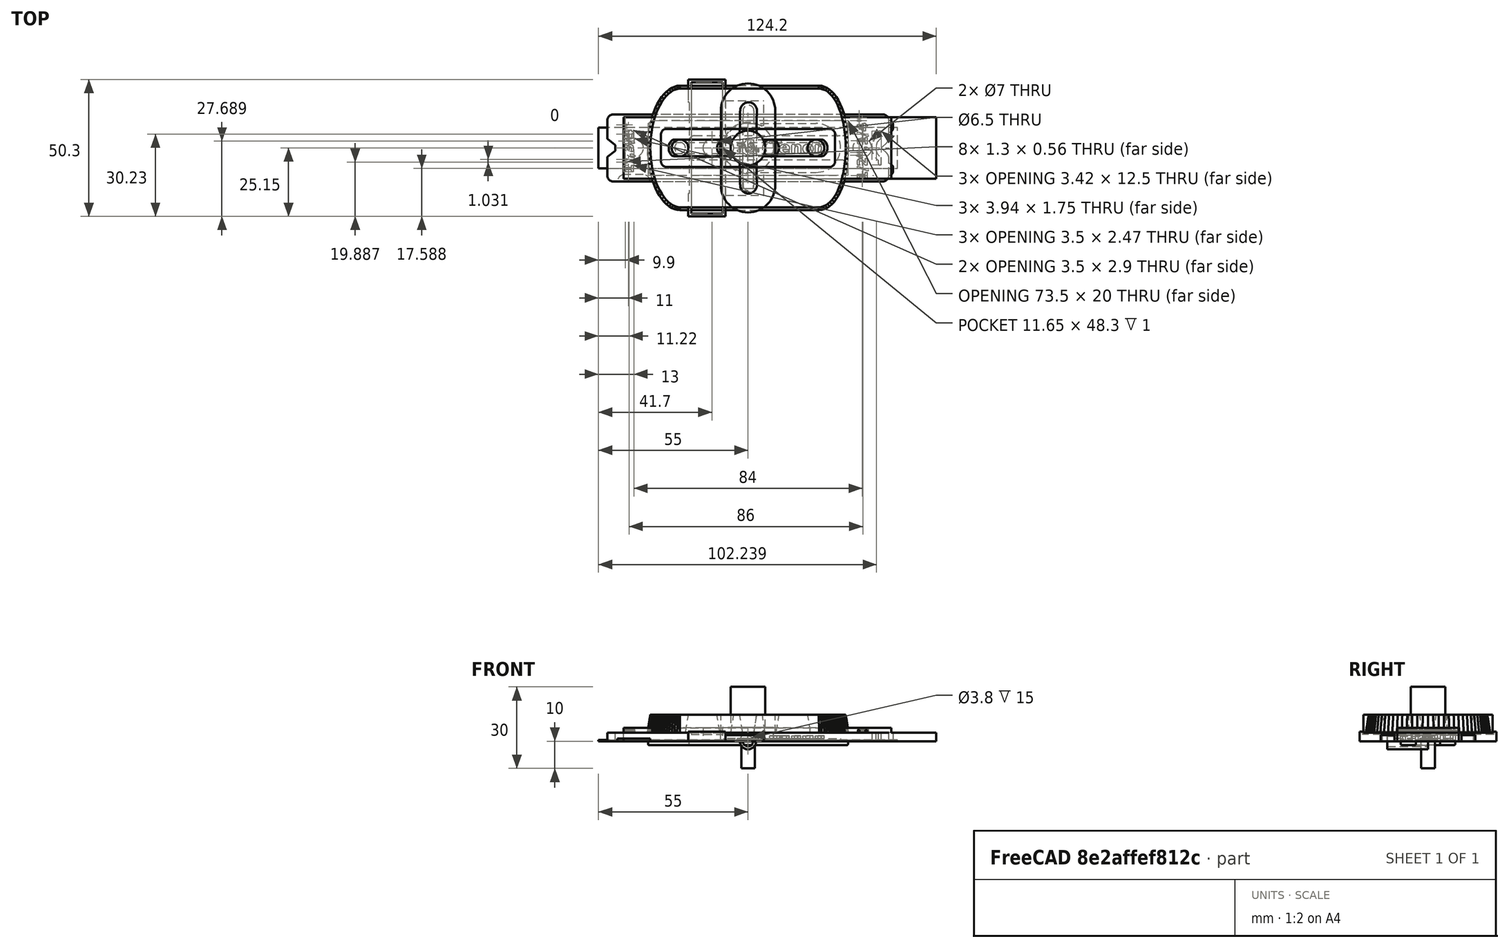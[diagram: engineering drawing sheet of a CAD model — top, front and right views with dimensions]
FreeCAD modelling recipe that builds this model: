
FCSTD DOCUMENT  (FreeCAD 1.1R20260325 (Git shallow))
Label: FMT Guide
License: All rights reserved
LicenseURL: http://en.wikipedia.org/wiki/All_rights_reserved
objects: Sketcher::SketchObject×25, PartDesign::Pad×16, App::Point×10, PartDesign::Body×10, PartDesign::Pocket×5, Part::Part2DObjectPython×4, Part::Extrusion×4, Part::Fuse×3, Part::MultiFuse×3, PartDesign::Plane×2, Part::Cut×2, Mesh::Feature×2, Spreadsheet::Sheet×1, Part::DatumPlane×1, PartDesign::Fillet×1, Part::Scale×1, Part::Loft×1, PartDesign::LinearPattern×1
note: 148 computed .brp shape members not serialized (recipe doc carries the construction recipe); baked Part::Feature solids carry a one-line shape summary decoded from their .brp

FEATURE [Sketcher::SketchObject] Sketch  label="Base Outline"
  ArcFitTolerance = 1e-06
  AttachmentSupport = -> [XY_Plane]
  ExternalTypes = [0]
  FullyConstrained = true
  MakeInternals = false
  MapMode = 5
  _ExternalGeoVersion = 0
  expr: Constraints[12] = Spreadsheet.Base_Corner_Radious
  expr: Constraints[18] = Spreadsheet.Base_Width
  expr: Constraints[19] = Spreadsheet.Base_Length
  sketch-geometry (32):
    g0: LineSegment StartX=-49.55 StartY=-12.32 StartZ=0 EndX=49.55 EndY=-12.32 EndZ=0
    g1: LineSegment [constr] StartX=51.75 StartY=-10.12 StartZ=0 EndX=51.75 EndY=10.12 EndZ=0
    g2: LineSegment StartX=49.55 StartY=12.32 StartZ=0 EndX=-49.55 EndY=12.32 EndZ=0
    g3: ArcOfCircle CenterX=-49.55 CenterY=10.12 CenterZ=0 NormalX=0 NormalY=0 NormalZ=1 AngleXU=0 Radius=2.2 StartAngle=1.5708 EndAngle=3.14159
    g4: ArcOfCircle CenterX=-49.55 CenterY=-10.12 CenterZ=0 NormalX=0 NormalY=0 NormalZ=1 AngleXU=0 Radius=2.2 StartAngle=3.14159 EndAngle=4.71239
    g5: ArcOfCircle CenterX=49.55 CenterY=-10.12 CenterZ=0 NormalX=0 NormalY=0 NormalZ=1 AngleXU=0 Radius=2.2 StartAngle=4.71239 EndAngle=6.28319
    g6: ArcOfCircle CenterX=49.55 CenterY=10.12 CenterZ=0 NormalX=0 NormalY=0 NormalZ=1 AngleXU=0 Radius=2.2 StartAngle=4e-16 EndAngle=1.5708
    g7: GeomPoint [constr] X=51.75 Y=-12.32 Z=0
    g8: LineSegment StartX=51.75 StartY=10.12 StartZ=0 EndX=51.75 EndY=3.625 EndZ=0
    g9: LineSegment StartX=51.75 StartY=-10.12 StartZ=0 EndX=51.75 EndY=-3.625 EndZ=0
    g10: ArcOfCircle CenterX=-49.55 CenterY=3.61127 CenterZ=0 NormalX=0 NormalY=0 NormalZ=1 AngleXU=0 Radius=2.2 StartAngle=3.14159 EndAngle=3.92699
    g11: ArcOfCircle CenterX=-49.55 CenterY=-3.61127 CenterZ=0 NormalX=0 NormalY=0 NormalZ=1 AngleXU=0 Radius=2.2 StartAngle=2.35619 EndAngle=3.14159
    g12: LineSegment StartX=51.5641 StartY=3.23597 StartZ=0 EndX=48.9359 EndY=1.11403 EndZ=0
    g13: LineSegment StartX=48.75 StartY=0.725 StartZ=0 EndX=48.75 EndY=-0.725 EndZ=0
    g14: LineSegment StartX=48.9359 StartY=-1.11403 StartZ=0 EndX=51.5641 EndY=-3.23597 EndZ=0
    g15: ArcOfCircle CenterX=51.25 CenterY=3.625 CenterZ=0 NormalX=0 NormalY=0 NormalZ=1 AngleXU=0 Radius=0.5 StartAngle=5.39161 EndAngle=6.28319
    g16: ArcOfCircle CenterX=51.25 CenterY=-3.625 CenterZ=0 NormalX=0 NormalY=0 NormalZ=1 AngleXU=0 Radius=0.5 StartAngle=6.28319 EndAngle=7.17476
    g17: ArcOfCircle CenterX=49.25 CenterY=-0.725 CenterZ=0 NormalX=0 NormalY=0 NormalZ=1 AngleXU=0 Radius=0.5 StartAngle=3.14159 EndAngle=4.03317
    g18: ArcOfCircle CenterX=49.25 CenterY=0.725 CenterZ=0 NormalX=0 NormalY=0 NormalZ=1 AngleXU=0 Radius=0.5 StartAngle=2.25002 EndAngle=3.14159
    g19: LineSegment StartX=-51.1056 StartY=2.05563 StartZ=0 EndX=-49.05 EndY=0 EndZ=0
    g20: LineSegment StartX=-49.05 StartY=0 StartZ=0 EndX=-51.1056 EndY=-2.05563 EndZ=0
    g21: LineSegment StartX=-48.95 StartY=5.75 StartZ=0 EndX=-48.95 EndY=3.5 EndZ=0
    g22: LineSegment StartX=-47.95 StartY=5.75 StartZ=0 EndX=-47.95 EndY=4.6 EndZ=0
    g23: ArcOfCircle CenterX=-48.45 CenterY=5.75 CenterZ=0 NormalX=0 NormalY=0 NormalZ=1 AngleXU=0 Radius=0.5 StartAngle=1e-16 EndAngle=3.14159
    g24: LineSegment StartX=-48.95 StartY=-3.5 StartZ=0 EndX=-48.95 EndY=-5.75 EndZ=0
    g25: LineSegment StartX=-47.95 StartY=-4.6 StartZ=0 EndX=-47.95 EndY=-5.75 EndZ=0
    g26: ArcOfCircle CenterX=-48.45 CenterY=-5.75 CenterZ=0 NormalX=0 NormalY=0 NormalZ=1 AngleXU=0 Radius=0.5 StartAngle=3.14159 EndAngle=6.28319
    g27: ArcOfCircle CenterX=-51.1056 CenterY=0 CenterZ=0 NormalX=0 NormalY=0 NormalZ=1 AngleXU=0 Radius=4.11057 StartAngle=5.26441 EndAngle=7.30196
    g28: ArcOfCircle CenterX=-51.1056 CenterY=0 CenterZ=0 NormalX=0 NormalY=0 NormalZ=1 AngleXU=0 Radius=5.57835 StartAngle=5.31366 EndAngle=7.25271
    g29: LineSegment StartX=-51.75 StartY=10.12 StartZ=0 EndX=-51.75 EndY=3.61127 EndZ=0
    g30: LineSegment StartX=-51.75 StartY=-3.61127 StartZ=0 EndX=-51.75 EndY=-10.12 EndZ=0
    g31: GeomPoint X=50.25 Y=2.175 Z=0
  constraints (79):
    c: Tangent(g0,g4) = -1.5708
    c: Tangent(g0,g5) = -1.5708
    c: Tangent(g1,g5) = -1.5708
    c: Tangent(g1,g6) = -1.5708
    c: Tangent(g2,g6) = -1.5708
    c: Tangent(g2,g3) = -1.5708
    c: Vertical(g1)
    c: Horizontal(g0)
    c: Horizontal(g2)
    c: Equal(g4,g5)
    c: PointOnObject(g7,g0)
    c: PointOnObject(g7,g1)
    c: Radius(g6) = 2.2
    c: Symmetric(g3,g6,g-2)
    c: Symmetric(g3,g4,g-1)
    c: Tangent(g6,g8)
    c: Coincident(g9,g1)
    c: Coincident(g8,g1)
    c: DistanceY(g0,g2) = 24.64
    c: DistanceX(g3,g1) = 103.5
    c: Equal(g3,g10)
    c: Tangent(g8,g15) = 1.5708
    c: Tangent(g12,g15) = 1.5708
    c: Tangent(g9,g16) = -1.5708
    c: Tangent(g14,g16) = 1.5708
    c: Tangent(g13,g17) = -1.5708
    c: Tangent(g14,g17) = -1.5708
    c: Tangent(g12,g18) = -1.5708
    c: Tangent(g13,g18) = -1.5708
    c: Equal(g15,g18)
    c: Equal(g18,g17)
    c: Equal(g17,g16)
    c: Radius(g15) = 0.5
    c: Symmetric(g18,g17,g-1)
    c: Symmetric(g15,g16,g-1)
    c: DistanceY(g16,g15) = 7.25
    c: DistanceY(g17,g18) = 1.45
    c: DistanceX(g18,g15) = 2
    c: Equal(g5,g6)
    c: PointOnObject(g19,g-1)
    c: Coincident(g20,g19)
    c: Angle(g19,g20) = 1.5708
    c: Tangent(g19,g10) = -1.5708
    c: Tangent(g20,g11) = -1.5708
    c: Symmetric(g10,g11,g-1)
    c: DistanceX(g10,g19) = 2.7
    c: Vertical(g21)
    c: Vertical(g22)
    c: Tangent(g23,g21) = -1.5708
    c: Tangent(g23,g22) = 1.5708
    c: Vertical(g22,g25)
    c: Vertical(g21,g24)
    c: Radius(g23) = 0.5
    c: Vertical(g24)
    c: Vertical(g25)
    c: Coincident(g26,g24)
    c: Coincident(g26,g25)
    c: Equal(g26,g23)
    c: Symmetric(g26,g23,g-1)
    c: Coincident(g27,g21)
    c: Coincident(g24,g27)
    c: PointOnObject(g27,g-1)
    c: Coincident(g28,g22)
    c: Coincident(g28,g25)
    c: Coincident(g27,g28)
    c: DistanceY(g26,g23) = 11.5
    c: DistanceX(g10,g23) = 3.3
    c: DistanceY(g21,g22) = 1.1
    c: DistanceY(g24,g21) = 7
    c: Vertical(g10,g27)
    c: Vertical(g30)
    c: Vertical(g29)
    c: Tangent(g10,g29) = -1.5708
    c: Tangent(g30,g11) = -1.5708
    c: Tangent(g3,g29) = -1.5708
    c: Tangent(g30,g4) = -1.5708
    c: DistanceY(g18,g15) = 2.9
    c: DistanceX(g19,g13) = 97.8
    c: Symmetric(g12,g12,g31)
FEATURE [Spreadsheet::Sheet] Spreadsheet
  cells = A1='Base; A2='Upper Title; B2(Upper_Title)='1",3/4"; A3='Lower Title; B3(Lower_Title)='1/2",1/4"; A4='Base Width; B4(Base_Width)=24.64; C4='Width of base of guide; A5='Base Length; B5(Base_Length)=103.5; C5='Length of base of guide; A6='Base Thickness; B6(Base_Thickness)=3.1; C6='Thickness of base of guide; A7='Base Corner Radious; B7(Base_Corner_Radious)=2.2; C7='Radii of base curves; A9='Lower Plane; B9(Lower_Plane)==Base_Thickness + 0.1; C9='Lower plane of guide portion; A10='Upper Plane; B10(Upper_Plane)==Lower_Plane + 6.5; C10='Upper plane of guide portion; A12='Pin Bottom Width; B12(Pin_Bottom_Width)=4; C12='Diameter of narrow point of Pin; A13='Pin Top Width; B13(Pin_Top_Width)=5; C13='Diameter of wide point of pin; A14='Pin Angle; B14(Pin_Angle)=9.22; A15='Calculated Pin Angle; B15==atan((Pin_Top_Width - Pin_Bottom_Width) / 3) / 2; A16='Bump Thickness; B16(Bump_Thickness)==Base_Thickness - 0.5; A17='Bump Width; B17(Bump_Width)=3.2; A18='Bump Spacing; B18(Bump_Spacing)=15.7; A19='Margin; B19(Margin)=1; A20='Pin Spacing; B20(Pin_Spacing)=250; A22='Mortise & Tenon; A23='Movement Ratio; B23(Movement_Ratio)=2; C23='Y-scale for guide; A24='Width; B24(Width)=12; C24='Width of tenon/mortise; A25='Length; B25(Length)=65; C25='Length of tenon/mortise; A26='Router Diameter; B26(Router_Diameter)==Width; C26='Always equals width of tenon; A27='Width Delta; B27(Width_Delta)=0; C27='Extra Tenon Width; A28='Length Delta; B28(Length_Delta)=0; C28='Extra Tenon Length; A29='Slot Delta; B29(Slot_Delta)=1.35; C29='Extra Mortise Length; A31='Dowel Centres; A32='Dowel Extent; B32(Dowel_Extent)=50; C32='Extent of Dowels; A33='Dowel Length; B33(Dowel_Length)==Dowel_Extent + 10; C33='Length of base (calculated); A34='Dowel Width; B34(Dowel_Width)=10; C34='Width of base; A35='Dowel Number; B35(Dowel_Number)=4; A37='Centering Disk; A38='Centering Title; B38(Centering_Title)='1/2"; A39='Centering Disk Diameter; B39(Centering_Disk_Diameter)=18.8; A40='Centering Disk Thickness; B40(Centering_Disk_Thickness)=5; A41='Centering Post Diameter; B41(Centering_Post_Diameter)=12.7; A42='Centering Post Length; B42(Centering_Post_Length)=10; A44='Y Tenon; A45='Tenon Base Width; B45(Tenon_Base_Width)=20; A46='Tenon Extra Length; B46(Tenon_Extra_Length)=20; A47='Y Tenon Length; B47(Y_Tenon_Length)=25.4; C47='Length of Y tenon; A48='Y Tenon Width; B48(Y_Tenon_Width)=12.7; C48='Width of tenon/Router Bit; A49='Y Slot Delta; B49(Y_Slot_Delta)=1; C49='Extra Mortise Length
FEATURE [PartDesign::Plane] DatumPlane  label="Upper Plane"
  AttachmentOffset = pos=(0,0,9.7) rot=(0,0,1;0rad)
  AttachmentSupport = -> [XY_Plane]
  Length = 60
  MapMode = 5
  Placement = pos=(0,0,9.7) rot=(0,0,1;0rad)
  ResizeMode = 0
  Width = 60
  expr: .AttachmentOffset.Base.z = Spreadsheet.Upper_Plane
FEATURE [PartDesign::Plane] DatumPlane001  label="Mid Plane"
  AttachmentOffset = pos=(0,0,3.2) rot=(0,0,1;0rad)
  AttachmentSupport = -> [XY_Plane]
  Length = 60
  MapMode = 5
  Placement = pos=(0,0,3.2) rot=(0,0,1;0rad)
  ResizeMode = 0
  Width = 60
  expr: .AttachmentOffset.Base.z = Spreadsheet.Lower_Plane
FEATURE [Part::DatumPlane] DatumPlane002  label="Base Surface Plane"
  AttachmentSupport = -> [Origin]
  Placement = pos=(0,0,3.1) rot=(0,0,1;0rad)
  expr: .Placement.Base.z = Spreadsheet.Base_Thickness
FEATURE [PartDesign::Pad] Pad  label="Base Base"
  Direction = (0,0,1)
  Length = 3.1
  Length2 = 10
  Profile = -> Sketch
  ReferenceAxis = -> Sketch [N_Axis]
  SideType = 0
  Suppressed = false
  Type = 0
  Type2 = 0
  expr: Length = Spreadsheet.Base_Thickness
FEATURE [Part::Part2DObjectPython] ShapeString001  label="Label"  # Draft 2D object (typed FeaturePython)
  FontFile = <path>
  Fuse = false
  Justification = 4
  JustificationReference = 0
  KeepLeftMargin = false
  MakeFace = true
  ObliqueAngle = 0
  Placement = pos=(44,0,3.1) rot=(0,0,1;4.71239rad)
  ScaleToSize = true
  Size = 3.5
  String = 1",3/4"
  Tracking = 0
  expr: .Placement.Base.z = Spreadsheet.Base_Thickness
  expr: String = Spreadsheet.Upper_Title
FEATURE [Part::Extrusion] Extrude  label="Extrude Upper"
  Base = -> ShapeString001
  Dir = (0,0,1)
  DirMode = 2
  FaceMakerClass = Part::FaceMakerBullseye
  FaceMakerMode = 3
  InnerWireTaper = 0
  LengthFwd = 1
  LengthRev = 0
  Solid = false
  Symmetric = false
FEATURE [App::Point] Origin007  label="Origin008"
  Role = Origin
FEATURE [Sketcher::SketchObject] Sketch008
  ArcFitTolerance = 1e-06
  AttachmentSupport = -> [Origin006]
  ExternalTypes = [0]
  FullyConstrained = true
  MakeInternals = false
  MapMode = 5
  _ExternalGeoVersion = 1
  expr: Constraints[1] = Spreadsheet.Centering_Disk_Diameter
  sketch-geometry (1):
    g0: Circle CenterX=0 CenterY=0 CenterZ=0 NormalX=0 NormalY=0 NormalZ=1 AngleXU=0 Radius=9.4
  constraints (2):
    c: Coincident(g0,g-1)
    c: Diameter(g0) = 18.8
FEATURE [PartDesign::Pad] Pad002  label="Base001"
  Direction = (0,0,1)
  Length = 5
  Length2 = 10
  Profile = -> Sketch008
  ReferenceAxis = -> Sketch008 [N_Axis]
  SideType = 0
  Suppressed = false
  Type = 0
  Type2 = 0
  expr: Length = Spreadsheet.Centering_Disk_Thickness
FEATURE [Sketcher::SketchObject] Sketch009
  ArcFitTolerance = 1e-06
  AttachmentSupport = -> [Pad002]
  ExternalTypes = [0]
  FullyConstrained = true
  MakeInternals = false
  MapMode = 5
  Placement = pos=(0,0,5) rot=(0,0,1;0rad)
  _ExternalGeoVersion = 1
  expr: Constraints[1] = Spreadsheet.Centering_Post_Diameter
  sketch-geometry (1):
    g0: Circle CenterX=0 CenterY=0 CenterZ=0 NormalX=0 NormalY=0 NormalZ=1 AngleXU=0 Radius=6.35
  constraints (2):
    c: Coincident(g0,g-1)
    c: Diameter(g0) = 12.7
FEATURE [PartDesign::Pad] Pad003  label="Arbor"
  BaseFeature = -> Pad002
  Direction = (0,0,1)
  Length = 15
  Length2 = 10
  Profile = -> Sketch009
  ReferenceAxis = -> Sketch009 [N_Axis]
  SideType = 0
  Suppressed = false
  Type = 0
  Type2 = 0
  expr: Length = Spreadsheet.Centering_Post_Length + Spreadsheet.Centering_Disk_Thickness
FEATURE [PartDesign::Body] Body003  label="Centering Bare"
  AllowCompound = false
  Group = -> [Sketch008,Pad002,Sketch009,Pad003]
  Origin = -> Origin006
  Tip = -> Pad003
FEATURE [Sketcher::SketchObject] Sketch013  label="Outline"
  ArcFitTolerance = 1e-06
  AttachmentSupport = -> [DatumPlane002]
  ExternalTypes = [0]
  FullyConstrained = true
  MakeInternals = false
  MapMode = 5
  Placement = pos=(0,0,3.1) rot=(0,0,1;0rad)
  _ExternalGeoVersion = 1
  expr: Constraints[18] = Spreadsheet.Dowel_Length
  expr: Constraints[19] = Spreadsheet.Dowel_Width
  sketch-geometry (10):
    g0: LineSegment StartX=-32 StartY=5 StartZ=0 EndX=-32 EndY=-5 EndZ=0
    g1: LineSegment StartX=-30 StartY=-7 StartZ=0 EndX=30 EndY=-7 EndZ=0
    g2: LineSegment StartX=32 StartY=-5 StartZ=0 EndX=32 EndY=5 EndZ=0
    g3: LineSegment StartX=30 StartY=7 StartZ=0 EndX=-30 EndY=7 EndZ=0
    g4: ArcOfCircle CenterX=-30 CenterY=5 CenterZ=0 NormalX=0 NormalY=0 NormalZ=1 AngleXU=0 Radius=2 StartAngle=1.5708 EndAngle=3.14159
    g5: ArcOfCircle CenterX=-30 CenterY=-5 CenterZ=0 NormalX=0 NormalY=0 NormalZ=1 AngleXU=0 Radius=2 StartAngle=3.14159 EndAngle=4.71239
    g6: ArcOfCircle CenterX=30 CenterY=-5 CenterZ=0 NormalX=0 NormalY=0 NormalZ=1 AngleXU=0 Radius=2 StartAngle=4.71239 EndAngle=6.28319
    g7: ArcOfCircle CenterX=30 CenterY=5 CenterZ=0 NormalX=0 NormalY=0 NormalZ=1 AngleXU=0 Radius=2 StartAngle=1e-16 EndAngle=1.5708
    g8: GeomPoint [constr] X=-32 Y=7 Z=0
    g9: GeomPoint [constr] X=32 Y=-7 Z=0
  constraints (22):
    c: Tangent(g0,g4) = -1.5708
    c: Tangent(g0,g5) = -1.5708
    c: Tangent(g1,g5) = -1.5708
    c: Tangent(g1,g6) = -1.5708
    c: Tangent(g2,g6) = -1.5708
    c: Tangent(g2,g7) = -1.5708
    c: Tangent(g3,g7) = -1.5708
    c: Tangent(g3,g4) = -1.5708
    c: Vertical(g0)
    c: Vertical(g2)
    c: Horizontal(g1)
    c: Horizontal(g3)
    c: Equal(g4,g5)
    c: PointOnObject(g8,g0)
    c: PointOnObject(g8,g3)
    c: PointOnObject(g9,g1)
    c: PointOnObject(g9,g2)
    c: Radius(g7) = 2
    c: DistanceX(g4,g7) = 60
    c: DistanceY(g6,g7) = 10
    c: Symmetric(g7,g6,g-1)
    c: Symmetric(g4,g7,g-2)
FEATURE [PartDesign::Pad] Pad004  label="Dowel Base"
  Direction = (0,0,1)
  Length = 6.6
  Length2 = 10
  Placement = pos=(0,0,3.1) rot=(0,0,1;0rad)
  Profile = -> Sketch013
  ReferenceAxis = -> Sketch013 [N_Axis]
  SideType = 0
  Suppressed = false
  Type = 0
  Type2 = 0
  expr: Length = Spreadsheet.Upper_Plane - Spreadsheet.Base_Thickness
FEATURE [App::Point] Origin009  label="Origin011"
  Role = Origin
FEATURE [App::Point] Origin002  label="Origin"
  Role = Origin
FEATURE [Part::Part2DObjectPython] ShapeString  # Draft 2D object (typed FeaturePython)
  FontFile = <path>
  Fuse = false
  Justification = 4
  JustificationReference = 0
  KeepLeftMargin = false
  MakeFace = true
  ObliqueAngle = 0
  Placement = pos=(0,0,0) rot=(1,0,0;3.14159rad)
  ScaleToSize = false
  Size = 3
  String = 1/2"
  Tracking = 0
  expr: String = Spreadsheet.Centering_Title
FEATURE [Part::Extrusion] Extrude001  label="Description"
  Base = -> ShapeString
  Dir = (0,0,-1)
  DirMode = 2
  FaceMakerClass = Part::FaceMakerBullseye
  FaceMakerMode = 3
  InnerWireTaper = 0
  LengthFwd = 1
  LengthRev = 0
  Reversed = true
  Solid = false
  Symmetric = false
FEATURE [Part::Part2DObjectPython] ShapeString002  # Draft 2D object (typed FeaturePython)
  FontFile = <path>
  Fuse = false
  Justification = 4
  JustificationReference = 0
  KeepLeftMargin = false
  MakeFace = true
  ObliqueAngle = 0
  Placement = pos=(-42,0,3.1) rot=(0,0,1;4.71239rad)
  ScaleToSize = true
  Size = 3.5
  String = 1/2",1/4"
  Tracking = 0
  expr: .Placement.Base.z = Spreadsheet.Base_Thickness
  expr: String = Spreadsheet.Lower_Title
FEATURE [Part::Extrusion] Extrude002  label="Extrude Lower"
  Base = -> ShapeString002
  Dir = (0,0,1)
  DirMode = 2
  FaceMakerClass = Part::FaceMakerBullseye
  FaceMakerMode = 3
  InnerWireTaper = 0
  LengthFwd = 1
  LengthRev = 0
  Solid = false
  Symmetric = false
FEATURE [Part::Fuse] Fusion006  label="UpperLowerLabel"
  Base = -> Extrude
  Tool = -> Extrude002
FEATURE [Part::Cut] Cut002  label="Centering"
  Base = -> Body003
  Tool = -> Extrude001
FEATURE [App::Point] Origin011  label="Origin013"
  Role = Origin
FEATURE [Sketcher::SketchObject] Sketch014  label="Tenon Surround Outline"
  ArcFitTolerance = 1e-06
  AttachmentSupport = -> [DatumPlane002]
  ExternalTypes = [0]
  FullyConstrained = true
  MakeInternals = false
  MapMode = 5
  Placement = pos=(0,0,3.1) rot=(0,0,1;0rad)
  _ExternalGeoVersion = 1
  expr: Constraints[7] = 2 * (Spreadsheet.Y_Tenon_Length - Spreadsheet.Y_Tenon_Width + Spreadsheet.Y_Slot_Delta)
  expr: Constraints[9] = Spreadsheet.Tenon_Base_Width / 2
  sketch-geometry (5):
    g0: GeomPoint [constr] X=0 Y=0 Z=0
    g1: ArcOfCircle CenterX=0 CenterY=13.7 CenterZ=0 NormalX=0 NormalY=0 NormalZ=1 AngleXU=0 Radius=10 StartAngle=7.7e-15 EndAngle=3.14159
    g2: ArcOfCircle CenterX=0 CenterY=-13.7 CenterZ=0 NormalX=0 NormalY=0 NormalZ=1 AngleXU=0 Radius=10 StartAngle=3.14159 EndAngle=6.28319
    g3: LineSegment StartX=10 StartY=13.7 StartZ=0 EndX=10 EndY=-13.7 EndZ=0
    g4: LineSegment StartX=-10 StartY=13.7 StartZ=0 EndX=-10 EndY=-13.7 EndZ=0
  constraints (10):
    c: Coincident(g0,g-1)
    c: Tangent(g1,g3) = 1.5708
    c: Tangent(g1,g4) = -1.5708
    c: Tangent(g2,g3) = 1.5708
    c: Tangent(g2,g4) = -1.5708
    c: Equal(g1,g2)
    c: Symmetric(g1,g2,g-1)
    c: DistanceY(g3,g3) = 27.4
    c: PointOnObject(g1,g-2)
    c: Radius(g1) = 10
FEATURE [PartDesign::Pad] Pad005  label="X Tenon Surround"
  Direction = (0,0,1)
  Length = 6.6
  Length2 = 10
  Placement = pos=(0,0,3.1) rot=(0,0,1;0rad)
  Profile = -> Sketch014
  ReferenceAxis = -> Sketch014 [N_Axis]
  SideType = 0
  Suppressed = false
  Type = 0
  Type2 = 0
  expr: Length = Spreadsheet.Upper_Plane - Spreadsheet.Base_Thickness
FEATURE [Sketcher::SketchObject] Sketch016  label="Y Tenon Outline"
  ArcFitTolerance = 1e-06
  AttachmentSupport = -> [DatumPlane002]
  ExternalTypes = [0]
  FullyConstrained = true
  MakeInternals = false
  MapMode = 5
  Placement = pos=(0,0,3.1) rot=(0,0,1;0rad)
  _ExternalGeoVersion = 1
  expr: Constraints[0] = Spreadsheet.Pin_Bottom_Width / 2
  expr: Constraints[24] = Spreadsheet.Y_Tenon_Length - Spreadsheet.Y_Tenon_Width + Spreadsheet.Y_Slot_Delta
  expr: Constraints[25] = Spreadsheet.Pin_Spacing / 2
  expr: Constraints[7] = Spreadsheet.Router_Diameter
  sketch-geometry (24):
    g0: ArcOfCircle CenterX=0.187831 CenterY=13.7 CenterZ=0 NormalX=0 NormalY=0 NormalZ=1 AngleXU=0 Radius=2 StartAngle=6.25577 EndAngle=9.39736
    g1: ArcOfCircle CenterX=0.187831 CenterY=-13.7 CenterZ=0 NormalX=0 NormalY=0 NormalZ=1 AngleXU=0 Radius=2 StartAngle=3.16901 EndAngle=6.3106
    g2: GeomPoint [constr] X=125 Y=0 Z=0
    g3: ArcOfCircle [constr] CenterX=125 CenterY=6.85 CenterZ=0 NormalX=0 NormalY=0 NormalZ=1 AngleXU=0 Radius=6 StartAngle=1e-16 EndAngle=3.14159
    g4: ArcOfCircle [constr] CenterX=125 CenterY=-6.85 CenterZ=0 NormalX=0 NormalY=0 NormalZ=1 AngleXU=0 Radius=6 StartAngle=3.14159 EndAngle=6.28319
    g5: LineSegment [constr] StartX=131 StartY=6.85 StartZ=0 EndX=131 EndY=-6.85 EndZ=0
    g6: LineSegment [constr] StartX=119 StartY=6.85 StartZ=0 EndX=119 EndY=-6.85 EndZ=0
    g7: Circle [constr] CenterX=125 CenterY=6.85 CenterZ=0 NormalX=0 NormalY=0 NormalZ=1 AngleXU=0 Radius=6
    g8: GeomPoint [constr] X=249.812 Y=0 Z=0
    g9: LineSegment [constr] StartX=0.187831 StartY=13.7 StartZ=0 EndX=125 EndY=6.85 EndZ=0
    g10: LineSegment [constr] StartX=125 StartY=6.85 StartZ=0 EndX=249.812 EndY=0 EndZ=0
    g11: LineSegment [constr] StartX=0 StartY=0 StartZ=0 EndX=125 EndY=0 EndZ=0
    g12: LineSegment [constr] StartX=125 StartY=0 StartZ=0 EndX=250 EndY=0 EndZ=0
    g13: LineSegment [constr] StartX=-1.81142 StartY=13.7548 StartZ=0 EndX=2.18708 EndY=13.6452 EndZ=0
    g14: LineSegment [constr] StartX=-1.81142 StartY=-13.7548 StartZ=0 EndX=2.18708 EndY=-13.6452 EndZ=0
    g15: Circle [constr] CenterX=0 CenterY=0 CenterZ=0 NormalX=0 NormalY=0 NormalZ=1 AngleXU=0 Radius=2
    g16: ArcOfCircle CenterX=499.718 CenterY=4.97e-14 CenterZ=0 NormalX=0 NormalY=0 NormalZ=1 AngleXU=0 Radius=497.718 StartAngle=3.11417 EndAngle=3.16901
    g17: GeomPoint [constr] X=2 Y=0 Z=0
    g18: ArcOfCircle CenterX=499.718 CenterY=5.236e-13 CenterZ=0 NormalX=0 NormalY=0 NormalZ=1 AngleXU=0 Radius=501.718 StartAngle=3.11417 EndAngle=3.16901
    g19: GeomPoint [constr] X=-2 Y=0 Z=0
    g20: GeomPoint [constr] X=125 Y=12.85 Z=0
    g21: GeomPoint [constr] X=125 Y=-12.85 Z=0
    g22: GeomPoint [constr] X=0 Y=15.6912 Z=0
    g23: GeomPoint [constr] X=0 Y=-15.6912 Z=0
  constraints (58):
    c: Radius(g0) = 2
    c: PointOnObject(g2,g-1)
    c: Tangent(g3,g5) = 1.5708
    c: Tangent(g3,g6) = -1.5708
    c: Tangent(g4,g5) = 1.5708
    c: Tangent(g4,g6) = -1.5708
    c: Equal(g3,g4)
    c: Diameter(g3) = 12
    c: Symmetric(g3,g4,g-1)
    c: Vertical(g3,g2)
    c: Equal(g7,g3)
    c: DistanceY(g1,g0) = 27.4
    c: PointOnObject(g8,g-1)
    c: Coincident(g9,g0)
    c: Coincident(g9,g7)
    c: Coincident(g10,g7)
    c: Coincident(g10,g8)
    c: Parallel(g10,g9)
    c: Coincident(g11,g2)
    c: Coincident(g12,g2)
    c: PointOnObject(g12,g-1)
    c: Equal(g12,g11)
    c: Equal(g11,g10)
    c: Equal(g10,g9)
    c: Distance(g3,g4) = 13.7
    c: Distance(g11) = 125
    c: Coincident(g11,g-1)
    c: Symmetric(g0,g1,g-1)
    c: Coincident(g13,g0)
    c: Coincident(g13,g0)
    c: PointOnObject(g0,g13)
    c: Symmetric(g0,g1,g-1)
    c: Coincident(g14,g1)
    c: Coincident(g14,g1)
    c: PointOnObject(g1,g14)
    c: Coincident(g15,g11)
    c: Equal(g15,g1)
    c: Coincident(g16,g1)
    c: Tangent(g16,g15)
    c: PointOnObject(g17,g16)
    c: PointOnObject(g17,g-1)
    c: Tangent(g16,g0) = 1.5708
    c: Coincident(g18,g0)
    c: Coincident(g18,g1)
    c: PointOnObject(g19,g18)
    c: PointOnObject(g19,g-1)
    c: Tangent(g18,g15)
    c: PointOnObject(g20,g3)
    c: PointOnObject(g21,g4)
    c: Vertical(g21,g4)
    c: Vertical(g4,g20)
    c: DistanceY(g21,g20) = 25.7
    c: Coincident(g7,g3)
    c: PointOnObject(g22,g0)
    c: PointOnObject(g23,g1)
    c: PointOnObject(g23,g-2)
    c: PointOnObject(g22,g-2)
    c: Distance(g22,g23) = 31.3823
FEATURE [Sketcher::SketchObject] Sketch019  label="Reinforcing Outline"
  ArcFitTolerance = 1e-06
  ExternalTypes = [0]
  FullyConstrained = true
  MakeInternals = false
  MapMode = 5
  Placement = pos=(0,0,0) rot=(1,0,0;3.14159rad)
  _ExternalGeoVersion = 1
  expr: Constraints[9] = Spreadsheet.Base_Length - 2 * 15
  sketch-geometry (24):
    g0: LineSegment StartX=-34.75 StartY=10 StartZ=0 EndX=34.75 EndY=10 EndZ=0
    g1: LineSegment StartX=36.75 StartY=8 StartZ=0 EndX=36.75 EndY=-8 EndZ=0
    g2: LineSegment StartX=34.75 StartY=-10 StartZ=0 EndX=-34.75 EndY=-10 EndZ=0
    g3: LineSegment StartX=-36.75 StartY=-8 StartZ=0 EndX=-36.75 EndY=-6.5 EndZ=0
    g4: LineSegment StartX=-34.75 StartY=-4.5 StartZ=0 EndX=19.75 EndY=-4.5 EndZ=0
    g5: LineSegment StartX=21.75 StartY=-2.5 StartZ=0 EndX=21.75 EndY=2.5 EndZ=0
    g6: LineSegment StartX=19.75 StartY=4.5 StartZ=0 EndX=-34.75 EndY=4.5 EndZ=0
    g7: LineSegment StartX=-36.75 StartY=6.5 StartZ=0 EndX=-36.75 EndY=8 EndZ=0
    g8: ArcOfCircle CenterX=34.75 CenterY=8 CenterZ=0 NormalX=0 NormalY=0 NormalZ=1 AngleXU=0 Radius=2 StartAngle=0 EndAngle=1.5708
    g9: GeomPoint [constr] X=36.75 Y=10 Z=0
    g10: ArcOfCircle CenterX=34.75 CenterY=-8 CenterZ=0 NormalX=0 NormalY=0 NormalZ=1 AngleXU=0 Radius=2 StartAngle=4.71239 EndAngle=6.28319
    g11: GeomPoint [constr] X=36.75 Y=-10 Z=0
    g12: ArcOfCircle CenterX=-34.75 CenterY=8 CenterZ=0 NormalX=0 NormalY=0 NormalZ=1 AngleXU=0 Radius=2 StartAngle=1.5708 EndAngle=3.14159
    g13: GeomPoint [constr] X=-36.75 Y=10 Z=0
    g14: ArcOfCircle CenterX=-34.75 CenterY=6.5 CenterZ=0 NormalX=0 NormalY=0 NormalZ=1 AngleXU=0 Radius=2 StartAngle=3.14159 EndAngle=4.71239
    g15: GeomPoint [constr] X=-36.75 Y=4.5 Z=0
    g16: ArcOfCircle CenterX=-34.75 CenterY=-6.5 CenterZ=0 NormalX=0 NormalY=0 NormalZ=1 AngleXU=0 Radius=2 StartAngle=1.5708 EndAngle=3.14159
    g17: GeomPoint [constr] X=-36.75 Y=-4.5 Z=0
    g18: ArcOfCircle CenterX=-34.75 CenterY=-8 CenterZ=0 NormalX=0 NormalY=0 NormalZ=1 AngleXU=0 Radius=2 StartAngle=3.14159 EndAngle=4.71239
    g19: GeomPoint [constr] X=-36.75 Y=-10 Z=0
    g20: ArcOfCircle CenterX=19.75 CenterY=2.5 CenterZ=0 NormalX=0 NormalY=0 NormalZ=1 AngleXU=0 Radius=2 StartAngle=2e-16 EndAngle=1.5708
    g21: GeomPoint [constr] X=21.75 Y=4.5 Z=0
    g22: ArcOfCircle CenterX=19.75 CenterY=-2.5 CenterZ=0 NormalX=0 NormalY=0 NormalZ=1 AngleXU=0 Radius=2 StartAngle=4.71239 EndAngle=6.28319
    g23: GeomPoint [constr] X=21.75 Y=-4.5 Z=0
  constraints (51):
    c: Horizontal(g4)
    c: Symmetric(g21,g23,g-1)
    c: Symmetric(g9,g11,g-1)
    c: Symmetric(g15,g17,g-1)
    c: Symmetric(g13,g19,g-1)
    c: Vertical(g7)
    c: Distance(g9,g11) = 20
    c: Distance(g23,g21) = 9
    c: Symmetric(g11,g19,g-2)
    c: DistanceX(g19,g11) = 73.5
    c: DistanceX(g23,g11) = 15
    c: PointOnObject(g9,g0)
    c: PointOnObject(g9,g1)
    c: Tangent(g0,g8) = 1.5708
    c: Tangent(g1,g8) = 1.5708
    c: PointOnObject(g11,g1)
    c: PointOnObject(g11,g2)
    c: Tangent(g1,g10) = 1.5708
    c: Tangent(g2,g10) = 1.5708
    c: PointOnObject(g13,g0)
    c: PointOnObject(g13,g7)
    c: Tangent(g0,g12) = 1.5708
    c: Tangent(g7,g12) = 1.5708
    c: PointOnObject(g15,g6)
    c: PointOnObject(g15,g7)
    c: Tangent(g6,g14) = 1.5708
    c: Tangent(g7,g14) = 1.5708
    c: PointOnObject(g17,g3)
    c: PointOnObject(g17,g4)
    c: Tangent(g3,g16) = 1.5708
    c: Tangent(g4,g16) = 1.5708
    c: PointOnObject(g19,g2)
    c: PointOnObject(g19,g3)
    c: Tangent(g2,g18) = 1.5708
    c: Tangent(g3,g18) = 1.5708
    c: PointOnObject(g21,g5)
    c: PointOnObject(g21,g6)
    c: Tangent(g5,g20) = -1.5708
    c: Tangent(g6,g20) = -1.5708
    c: PointOnObject(g23,g4)
    c: PointOnObject(g23,g5)
    c: Tangent(g4,g22) = -1.5708
    c: Tangent(g5,g22) = -1.5708
    c: Equal(g8,g12)
    c: Equal(g12,g14)
    c: Equal(g14,g16)
    c: Equal(g16,g18)
    c: Equal(g18,g20)
    c: Equal(g20,g22)
    c: Equal(g22,g10)
    c: Radius(g10) = 2
FEATURE [PartDesign::Pad] Pad007  label="Reinforcing"
  BaseFeature = -> Pad
  Direction = (0,-1e-16,-1)
  Length = 1.5
  Length2 = 10
  Profile = -> Sketch019
  ReferenceAxis = -> Sketch019 [N_Axis]
  SideType = 0
  Suppressed = false
  Type = 0
  Type2 = 0
FEATURE [PartDesign::Fillet] Fillet002  label="Reinforcing Fillet"
  Base = -> Pad007 [Face48]
  BaseFeature = -> Pad007
  Radius = 0.5
  SupportTransform = false
  Suppressed = false
  UseAllEdges = false
FEATURE [Sketcher::SketchObject] Sketch020
  ArcFitTolerance = 1e-06
  AttachmentSupport = -> [Fillet002]
  ExternalTypes = [0]
  FullyConstrained = true
  MakeInternals = false
  MapMode = 5
  Placement = pos=(0,0,0) rot=(1,0,0;3.14159rad)
  _ExternalGeoVersion = 1
  expr: Constraints[7] = -Spreadsheet.Base_Width / 2
  sketch-geometry (4):
    g0: ArcOfCircle CenterX=38.5 CenterY=-12.32 CenterZ=0 NormalX=0 NormalY=0 NormalZ=1 AngleXU=0 Radius=2.5 StartAngle=1.5708 EndAngle=4.71239
    g1: ArcOfCircle CenterX=45.5 CenterY=-12.32 CenterZ=0 NormalX=0 NormalY=0 NormalZ=1 AngleXU=0 Radius=2.5 StartAngle=4.71239 EndAngle=7.85398
    g2: LineSegment StartX=38.5 StartY=-9.82 StartZ=0 EndX=45.5 EndY=-9.82 EndZ=0
    g3: LineSegment StartX=38.5 StartY=-14.82 StartZ=0 EndX=45.5 EndY=-14.82 EndZ=0
  constraints (10):
    c: Tangent(g0,g2) = 1.5708
    c: Tangent(g0,g3) = -1.5708
    c: Tangent(g1,g2) = 1.5708
    c: Tangent(g1,g3) = -1.5708
    c: Equal(g0,g1)
    c: Horizontal(g2)
    c: Radius(g1) = 2.5
    c: DistanceY(g0) = -12.32
    c: DistanceX(g0,g1) = 7
    c: DistanceX(g0) = 38.5
FEATURE [PartDesign::Pocket] Pocket  label="Recess"
  BaseFeature = -> Fillet002
  Direction = (0,0,1)
  Length = 1
  Length2 = 5
  Profile = -> Sketch020
  ReferenceAxis = -> Sketch020 [N_Axis]
  SideType = 0
  Suppressed = false
  Type = 0
  Type2 = 0
FEATURE [Sketcher::SketchObject] Sketch005  label="Slot Outline"
  ArcFitTolerance = 1e-06
  AttacherType = Attacher::AttachEngine3D
  ExternalTypes = [0]
  FullyConstrained = false
  MakeInternals = false
  MapMode = 5
  Placement = pos=(0,0,3.1) rot=(0,0,1;0rad)
  _ExternalGeoVersion = 1
  expr: .Placement.Base.z = Spreadsheet.Base_Thickness
  expr: Constraints[24] = Spreadsheet.Length - Spreadsheet.Router_Diameter + Spreadsheet.Pin_Top_Width
  expr: Constraints[7] = Spreadsheet.Length - Spreadsheet.Router_Diameter + Spreadsheet.Slot_Delta
  expr: Constraints[8] = Spreadsheet.Pin_Bottom_Width / 2
  sketch-geometry (11):
    g0: ArcOfCircle CenterX=-27.175 CenterY=0 CenterZ=0 NormalX=0 NormalY=0 NormalZ=1 AngleXU=0 Radius=2 StartAngle=1.5708 EndAngle=4.71239
    g1: ArcOfCircle CenterX=27.175 CenterY=0 CenterZ=0 NormalX=0 NormalY=0 NormalZ=1 AngleXU=0 Radius=2 StartAngle=4.71239 EndAngle=7.85398
    g2: LineSegment StartX=-27.175 StartY=2 StartZ=0 EndX=27.175 EndY=2 EndZ=0
    g3: LineSegment StartX=-27.175 StartY=-2 StartZ=0 EndX=27.175 EndY=-2 EndZ=0
    g4: GeomPoint X=-29.175 Y=0 Z=0
    g5: GeomPoint X=29.175 Y=0 Z=0
    g6: LineSegment [constr] StartX=-29 StartY=29.5438 StartZ=0 EndX=-29 EndY=17.568 EndZ=0
    g7: LineSegment [constr] StartX=-29 StartY=17.568 StartZ=0 EndX=29 EndY=17.568 EndZ=0
    g8: LineSegment [constr] StartX=29 StartY=17.568 StartZ=0 EndX=29 EndY=29.5438 EndZ=0
    g9: LineSegment [constr] StartX=29 StartY=29.5438 StartZ=0 EndX=-29 EndY=29.5438 EndZ=0
    g10: GeomPoint [constr] X=2e-16 Y=23.5559 Z=0
  constraints (25):
    c: Tangent(g0,g2) = 1.5708
    c: Tangent(g0,g3) = -1.5708
    c: Tangent(g1,g2) = 1.5708
    c: Tangent(g1,g3) = -1.5708
    c: Equal(g0,g1)
    c: PointOnObject(g0,g-1)
    c: Symmetric(g0,g1,g-2)
    c: Distance(g1,g0) = 54.35
    c: Radius(g1) = 2
    c: PointOnObject(g4,g0)
    c: PointOnObject(g5,g1)
    c: PointOnObject(g4,g-1)
    c: PointOnObject(g5,g-1)
    c: DistanceX(g4,g5) = 58.35
    c: Coincident(g6,g7)
    c: Coincident(g7,g8)
    c: Coincident(g8,g9)
    c: Coincident(g9,g6)
    c: Vertical(g6)
    c: Vertical(g8)
    c: Horizontal(g7)
    c: Horizontal(g9)
    c: Symmetric(g8,g6,g10)
    c: PointOnObject(g10,g-2)
    c: DistanceX(g9,g9) = 58
FEATURE [Part::Scale] Scale  label="Scaled Slot Outline"
  Base = -> Sketch005
  Placement = pos=(0,0,9.7) rot=(0,0,1;0rad)
  Uniform = false
  UniformScale = 1
  XScale = 1
  YScale = 1.5
  ZScale = 1
  expr: .Placement.Base.z = Spreadsheet.Upper_Plane
  expr: YScale = 6 / 4
FEATURE [Part::Loft] Loft  label="Slot (Loft)"
  Closed = false
  MaxDegree = 5
  Ruled = false
  Sections = -> [Sketch005,Scale]
  Solid = true
FEATURE [App::Point] Origin013  label="Origin016"
  Role = Origin
FEATURE [Sketcher::SketchObject] Sketch021
  ArcFitTolerance = 1e-06
  AttachmentSupport = -> [Origin012]
  ExternalTypes = [0]
  FullyConstrained = true
  MakeInternals = false
  MapMode = 5
  _ExternalGeoVersion = 1
  sketch-geometry (4):
    g0: ArcOfCircle CenterX=0 CenterY=0 CenterZ=0 NormalX=0 NormalY=0 NormalZ=1 AngleXU=0 Radius=9 StartAngle=1.5708 EndAngle=4.71239
    g1: ArcOfCircle CenterX=25 CenterY=0 CenterZ=0 NormalX=0 NormalY=0 NormalZ=1 AngleXU=0 Radius=9 StartAngle=4.71239 EndAngle=7.85398
    g2: LineSegment StartX=-4.34e-14 StartY=9 StartZ=0 EndX=25 EndY=9 EndZ=0
    g3: LineSegment StartX=6.3e-15 StartY=-9 StartZ=0 EndX=25 EndY=-9 EndZ=0
  constraints (9):
    c: Tangent(g0,g2) = 1.5708
    c: Tangent(g0,g3) = -1.5708
    c: Tangent(g1,g2) = 1.5708
    c: Tangent(g1,g3) = -1.5708
    c: Equal(g0,g1)
    c: PointOnObject(g1,g-1)
    c: Radius(g1) = 9
    c: Coincident(g0,g-1)
    c: DistanceX(g0,g1) = 25
FEATURE [PartDesign::Pad] Pad008
  Direction = (0,0,1)
  Length = 1
  Length2 = 10
  Profile = -> Sketch021
  ReferenceAxis = -> Sketch021 [N_Axis]
  SideType = 0
  Suppressed = false
  Type = 0
  Type2 = 0
FEATURE [Sketcher::SketchObject] Sketch022
  ArcFitTolerance = 1e-06
  AttachmentSupport = -> [Origin012]
  ExternalTypes = [0]
  FullyConstrained = true
  MakeInternals = false
  MapMode = 5
  _ExternalGeoVersion = 1
  sketch-geometry (1):
    g0: Circle CenterX=0 CenterY=0 CenterZ=0 NormalX=0 NormalY=0 NormalZ=1 AngleXU=0 Radius=2.5
  constraints (2):
    c: Coincident(g0,g-1)
    c: Diameter(g0) = 5
FEATURE [Sketcher::SketchObject] Sketch023
  ArcFitTolerance = 1e-06
  AttachmentSupport = -> [Origin012]
  ExternalTypes = [0]
  FullyConstrained = false
  MakeInternals = false
  MapMode = 5
  _ExternalGeoVersion = 1
  sketch-geometry (1):
    g0: Circle CenterX=0 CenterY=0 CenterZ=0 NormalX=0 NormalY=0 NormalZ=1 AngleXU=0 Radius=17.5985
  constraints (1):
    c: Coincident(g0,g-1)
FEATURE [Sketcher::SketchObject] Sketch024  label="Tenon Check"
  ArcFitTolerance = 1e-06
  ExternalTypes = [0]
  FullyConstrained = true
  MakeInternals = false
  _ExternalGeoVersion = 1
  sketch-geometry (13):
    g0: GeomPoint [constr] X=-50 Y=0 Z=0
    g1: GeomPoint [constr] X=50 Y=0 Z=0
    g2: ArcOfCircle [constr] CenterX=-10 CenterY=0 CenterZ=0 NormalX=0 NormalY=0 NormalZ=1 AngleXU=0 Radius=3 StartAngle=1.5708 EndAngle=4.71239
    g3: ArcOfCircle [constr] CenterX=10 CenterY=0 CenterZ=0 NormalX=0 NormalY=0 NormalZ=1 AngleXU=0 Radius=3 StartAngle=4.71239 EndAngle=7.85398
    g4: LineSegment [constr] StartX=-10 StartY=3 StartZ=0 EndX=10 EndY=3 EndZ=0
    g5: LineSegment [constr] StartX=-10 StartY=-3 StartZ=0 EndX=10 EndY=-3 EndZ=0
    g6: Circle [constr] CenterX=0 CenterY=6 CenterZ=0 NormalX=0 NormalY=0 NormalZ=1 AngleXU=0 Radius=3
    g7: ArcOfCircle CenterX=-60 CenterY=0 CenterZ=0 NormalX=0 NormalY=0 NormalZ=1 AngleXU=0 Radius=10 StartAngle=1.5708 EndAngle=4.71239
    g8: ArcOfCircle CenterX=-40 CenterY=0 CenterZ=0 NormalX=0 NormalY=0 NormalZ=1 AngleXU=0 Radius=10 StartAngle=4.71239 EndAngle=7.85398
    g9: LineSegment StartX=-60 StartY=10 StartZ=0 EndX=-40 EndY=10 EndZ=0
    g10: LineSegment StartX=-60 StartY=-10 StartZ=0 EndX=-40 EndY=-10 EndZ=0
    g11: Circle CenterX=-50 CenterY=12 CenterZ=0 NormalX=0 NormalY=0 NormalZ=1 AngleXU=0 Radius=2
    g12: LineSegment [constr] StartX=50 StartY=0 StartZ=0 EndX=-50 EndY=12 EndZ=0
  constraints (32):
    c: PointOnObject(g0,g-1)
    c: Symmetric(g0,g1,g-2)
    c: DistanceX(g0,g1) = 100
    c: Tangent(g2,g4) = 1.5708
    c: Tangent(g2,g5) = -1.5708
    c: Tangent(g3,g4) = 1.5708
    c: Tangent(g3,g5) = -1.5708
    c: Equal(g2,g3)
    c: PointOnObject(g2,g-1)
    c: Symmetric(g2,g3,g-2)
    c: Tangent(g6,g4)
    c: PointOnObject(g6,g-2)
    c: Tangent(g7,g9) = 1.5708
    c: Tangent(g7,g10) = -1.5708
    c: Tangent(g8,g9) = 1.5708
    c: Tangent(g8,g10) = -1.5708
    c: Equal(g7,g8)
    c: PointOnObject(g7,g-1)
    c: Equal(g10,g5)
    c: Symmetric(g7,g8,g0)
    c: DistanceX(g5,g5) = 20
    c: Diameter(g3) = 6
    c: Diameter(g11) = 4
    c: Tangent(g11,g9)
    c: Coincident(g12,g1)
    c: PointOnObject(g6,g12)
    c: Vertical(g12,g0)
    c: Coincident(g11,g12)
    c: DistanceY(g7,g7) = 20
    c: DistanceY(g7,g7) = 10
    c: Equal(g6,g3)
    c: DistanceY(g11) = 12
FEATURE [Part::Part2DObjectPython] ShapeString003  label="Tenon Text"  # Draft 2D object (typed FeaturePython)
  FontFile = <path>
  Fuse = false
  Justification = 6
  JustificationReference = 0
  KeepLeftMargin = false
  MakeFace = true
  ObliqueAngle = 0
  Placement = pos=(8,-2,1) rot=(0,0,1;0rad)
  ScaleToSize = true
  Size = 4.5
  String = Tenon
  Tracking = 0
FEATURE [Sketcher::SketchObject] Sketch025  label="Dowel Lower Outline"
  ArcFitTolerance = 1e-06
  AttachmentSupport = -> [DatumPlane002]
  ExternalTypes = [0]
  FullyConstrained = true
  MakeInternals = false
  MapMode = 5
  Placement = pos=(0,0,3.1) rot=(0,0,1;0rad)
  _ExternalGeoVersion = 1
  expr: Constraints[1] = Spreadsheet.Dowel_Extent / 2
  expr: Constraints[2] = Spreadsheet.Pin_Bottom_Width
  sketch-geometry (1):
    g0: Circle CenterX=-25 CenterY=0 CenterZ=0 NormalX=0 NormalY=0 NormalZ=1 AngleXU=0 Radius=2
  constraints (3):
    c: PointOnObject(g0,g-1)
    c: DistanceX(g0,g-1) = 25
    c: Diameter(g0) = 4
FEATURE [PartDesign::Pocket] Pocket001  label="Dowel Lower"
  BaseFeature = -> Pad004
  Direction = (0,0,-1)
  Length = 6.6
  Length2 = 5
  Placement = pos=(0,0,3.1) rot=(0,0,1;0rad)
  Profile = -> Sketch025
  ReferenceAxis = -> Sketch025 [N_Axis]
  Reversed = true
  SideType = 0
  Suppressed = false
  TaperAngle = 9.22
  Type = 0
  Type2 = 0
  expr: Length = Spreadsheet.Upper_Plane - Spreadsheet.Base_Thickness
  expr: TaperAngle = Spreadsheet.Pin_Angle
FEATURE [PartDesign::LinearPattern] LinearPattern
  BaseFeature = -> Pocket001
  Direction = -> Sketch025 [H_Axis]
  Direction2 = -> Sketch025 [V_Axis]
  Length = 50
  Length2 = 100
  Mode = 0
  Mode2 = 0
  Occurrences = 4
  Occurrences2 = 1
  Offset = 16.6667
  Offset2 = 100
  Originals = -> [Pocket001]
  Placement = pos=(0,0,3.1) rot=(0,0,1;0rad)
  Reversed2 = false
  SpacingPattern = [0]
  SpacingPattern2 = [0]
  Spacings = [-1,-1,-1]
  Suppressed = false
  TransformMode = 0
  expr: Length = Spreadsheet.Dowel_Extent
  expr: Occurrences = Spreadsheet.Dowel_Number
FEATURE [PartDesign::Body] Body004  label="Dowel Guide"
  AllowCompound = false
  Group = -> [Sketch013,Pad004,Sketch025,Pocket001,LinearPattern]
  Origin = -> Origin008
  Tip = -> LinearPattern
FEATURE [Part::Extrusion] Extrude004  label="Tenon Text Extrude"
  Base = -> ShapeString003
  Dir = (0,0,1)
  DirMode = 2
  FaceMakerClass = Part::FaceMakerBullseye
  FaceMakerMode = 3
  InnerWireTaper = 0
  LengthFwd = 1
  LengthRev = 0
  Solid = true
  Symmetric = false
FEATURE [PartDesign::Pocket] Pocket002  label="Y Tenon Template"
  BaseFeature = -> Pad005
  Direction = (0,0,-1)
  Length = 6.6
  Length2 = 5
  Placement = pos=(0,0,3.1) rot=(0,0,1;0rad)
  Profile = -> Sketch016
  ReferenceAxis = -> Sketch016 [N_Axis]
  Reversed = true
  SideType = 0
  Suppressed = false
  TaperAngle = 9.22
  Type = 0
  Type2 = 0
  expr: Length = Spreadsheet.Upper_Plane - Spreadsheet.Base_Thickness
  expr: TaperAngle = Spreadsheet.Pin_Angle
FEATURE [PartDesign::Body] Body005  label="Y Tenon Guide"
  AllowCompound = true
  Group = -> [Pad005,Sketch014,Sketch016,Pocket002]
  Origin = -> Origin010
  Tip = -> Pocket002
FEATURE [PartDesign::Pad] Pad010
  BaseFeature = -> Pad008
  Direction = (0,0,1)
  Length = 10
  Length2 = 10
  Profile = -> Sketch022
  ReferenceAxis = -> Sketch022 [N_Axis]
  Reversed = true
  SideType = 0
  Suppressed = false
  Type = 0
  Type2 = 0
FEATURE [PartDesign::Body] Body006  label="Router Depth Base"
  AllowCompound = false
  Group = -> [Sketch021,Pad008,Sketch022,Sketch023,Pad010]
  Origin = -> Origin012
  Tip = -> Pad010
FEATURE [Part::MultiFuse] Fusion010  label="Tenon Depth Guide"
  Shapes = -> [Body006,Extrude004]
FEATURE [Sketcher::SketchObject] Sketch026  label="Bump Outline"
  ArcFitTolerance = 1e-06
  AttachmentSupport = -> [DatumPlane002]
  ExternalGeometry = -> [Sketch]
  ExternalTypes = [0,0]
  FullyConstrained = true
  MakeInternals = false
  MapMode = 5
  Placement = pos=(0,0,3.1) rot=(0,0,1;0rad)
  _ExternalGeoVersion = 1
  expr: Constraints[13] = Spreadsheet.Bump_Width / 2
  expr: Constraints[15] = -Spreadsheet.Base_Length / 2
  sketch-geometry (9):
    g0: ArcOfCircle CenterX=-51.75 CenterY=8.52 CenterZ=0 NormalX=0 NormalY=0 NormalZ=1 AngleXU=0 Radius=1.6 StartAngle=1e-16 EndAngle=3.14159
    g1: ArcOfCircle CenterX=-51.75 CenterY=7.35 CenterZ=0 NormalX=0 NormalY=0 NormalZ=1 AngleXU=0 Radius=1.6 StartAngle=3.14159 EndAngle=6.28319
    g2: LineSegment StartX=-50.15 StartY=8.52 StartZ=0 EndX=-50.15 EndY=7.35 EndZ=0
    g3: LineSegment StartX=-53.35 StartY=8.52 StartZ=0 EndX=-53.35 EndY=7.35 EndZ=0
    g4: ArcOfCircle CenterX=-51.75 CenterY=-7.35 CenterZ=0 NormalX=0 NormalY=0 NormalZ=1 AngleXU=0 Radius=1.6 StartAngle=0 EndAngle=3.14159
    g5: ArcOfCircle CenterX=-51.75 CenterY=-8.52 CenterZ=0 NormalX=0 NormalY=0 NormalZ=1 AngleXU=0 Radius=1.6 StartAngle=3.14159 EndAngle=6.28319
    g6: LineSegment StartX=-50.15 StartY=-7.35 StartZ=0 EndX=-50.15 EndY=-8.52 EndZ=0
    g7: LineSegment StartX=-53.35 StartY=-7.35 StartZ=0 EndX=-53.35 EndY=-8.52 EndZ=0
    g8: GeomPoint X=-51.75 Y=5.75 Z=0
  constraints (20):
    c: Tangent(g0,g2) = 1.5708
    c: Tangent(g0,g3) = -1.5708
    c: Tangent(g1,g2) = 1.5708
    c: Tangent(g1,g3) = -1.5708
    c: Equal(g0,g1)
    c: Vertical(g2)
    c: Tangent(g4,g6) = 1.5708
    c: Tangent(g4,g7) = -1.5708
    c: Tangent(g5,g6) = 1.5708
    c: Tangent(g5,g7) = -1.5708
    c: Equal(g4,g5)
    c: Symmetric(g1,g4,g-1)
    c: Equal(g4,g0)
    c: Radius(g0) = 1.6
    c: Symmetric(g0,g5,g-1)
    c: DistanceX(g1) = -51.75
    c: PointOnObject(g8,g1)
    c: Vertical(g8,g1)
    c: Horizontal(g8,g-3)
    c: PointOnObject(g-4,g0)
FEATURE [PartDesign::Pad] Pad011  label="Bump"
  BaseFeature = -> Pocket
  Direction = (0,0,1)
  Length = 2.6
  Length2 = 10
  Profile = -> Sketch026
  ReferenceAxis = -> Sketch026 [N_Axis]
  Reversed = true
  SideType = 0
  Suppressed = false
  Type = 0
  Type2 = 0
  expr: Length = Spreadsheet.Bump_Thickness
FEATURE [PartDesign::Body] Body  label="Base"
  AllowCompound = false
  Group = -> [Sketch,Pad,Sketch019,Pad007,Fillet002,Sketch020,Pocket,Sketch026,Pad011]
  Origin = -> Origin
  Tip = -> Pad011
FEATURE [Part::MultiFuse] Fusion007  label="Base with Text"
  Placement = pos=(0,0,0) rot=(0,0,1;3.14159rad)
  Shapes = -> [Fusion006,Body]
FEATURE [Part::MultiFuse] Fusion  label="Dowling Guides"
  Shapes = -> [Body004,Fusion007]
FEATURE [App::Point] Origin015  label="Origin019"
  Role = Origin
FEATURE [Sketcher::SketchObject] Sketch027
  ArcFitTolerance = 1e-06
  AttachmentSupport = -> [Origin014]
  ExternalTypes = [0]
  FullyConstrained = true
  MakeInternals = false
  MapMode = 5
  Placement = pos=(0,0,0) rot=(1,0,0;1.5708rad)
  _ExternalGeoVersion = 1
  sketch-geometry (2):
    g0: Circle CenterX=0 CenterY=0 CenterZ=0 NormalX=0 NormalY=0 NormalZ=1 AngleXU=0 Radius=1.9
    g1: Circle CenterX=0 CenterY=0 CenterZ=0 NormalX=0 NormalY=0 NormalZ=1 AngleXU=0 Radius=3
  constraints (4):
    c: Coincident(g0,g-1)
    c: Coincident(g1,g0)
    c: Diameter(g1) = 6
    c: Diameter(g0) = 3.8
FEATURE [PartDesign::Pad] Pad012
  Direction = (0,-1,0)
  Length = 15
  Length2 = 10
  Profile = -> Sketch027
  ReferenceAxis = -> Sketch027 [N_Axis]
  SideType = 0
  Suppressed = false
  Type = 0
  Type2 = 0
FEATURE [PartDesign::Body] Body007  label="Depth Gauge Cylinder"
  AllowCompound = false
  Group = -> [Sketch027,Pad012]
  Origin = -> Origin014
  Tip = -> Pad012
FEATURE [App::Point] Origin017  label="Origin022"
  Role = Origin
FEATURE [Sketcher::SketchObject] Sketch028  label="Tab Outline"
  ArcFitTolerance = 1e-06
  AttachmentSupport = -> [Origin016]
  ExternalTypes = [0]
  FullyConstrained = true
  MakeInternals = false
  MapMode = 5
  _ExternalGeoVersion = 1
  sketch-geometry (8):
    g0: LineSegment StartX=-9.2 StartY=-17.45 StartZ=0 EndX=5.8 EndY=-17.45 EndZ=0
    g1: LineSegment StartX=5.8 StartY=-17.45 StartZ=0 EndX=5.8 EndY=-8.225 EndZ=0
    g2: LineSegment StartX=5.8 StartY=-8.225 StartZ=0 EndX=0 EndY=-9.225 EndZ=0
    g3: LineSegment StartX=0 StartY=-9.225 StartZ=0 EndX=0 EndY=9.225 EndZ=0
    g4: LineSegment StartX=0 StartY=9.225 StartZ=0 EndX=5.8 EndY=8.225 EndZ=0
    g5: LineSegment StartX=5.8 StartY=8.225 StartZ=0 EndX=5.8 EndY=17.45 EndZ=0
    g6: LineSegment StartX=-9.2 StartY=17.45 StartZ=0 EndX=5.8 EndY=17.45 EndZ=0
    g7: LineSegment StartX=-9.2 StartY=17.45 StartZ=0 EndX=-9.2 EndY=-17.45 EndZ=0
  constraints (20):
    c: Coincident(g0,g1)
    c: Coincident(g1,g2)
    c: Coincident(g2,g3)
    c: Coincident(g3,g4)
    c: Coincident(g4,g5)
    c: Vertical(g5)
    c: Symmetric(g3,g2,g-1)
    c: Symmetric(g4,g1,g-1)
    c: Horizontal(g0)
    c: Coincident(g6,g5)
    c: Symmetric(g5,g0,g-1)
    c: Symmetric(g6,g0,g-1)
    c: DistanceY(g0,g5) = 34.9
    c: DistanceY(g1,g4) = 16.45
    c: PointOnObject(g-1,g3)
    c: DistanceY(g3,g3) = 18.45
    c: Coincident(g7,g6)
    c: Coincident(g7,g0)
    c: DistanceX(g4) = 5.8
    c: DistanceX(g6,g6) = 15
FEATURE [PartDesign::Pad] Pad013
  Direction = (0,0,1)
  Length = 2.2
  Length2 = 10
  Profile = -> Sketch028
  ReferenceAxis = -> Sketch028 [N_Axis]
  SideType = 0
  Suppressed = false
  Type = 0
  Type2 = 0
FEATURE [Sketcher::SketchObject] Sketch030  label="Spacer Outline"
  ArcFitTolerance = 1e-06
  AttachmentSupport = -> [Origin016]
  ExternalTypes = [0]
  FullyConstrained = true
  MakeInternals = false
  MapMode = 5
  _ExternalGeoVersion = 1
  sketch-geometry (8):
    g0: LineSegment StartX=-22 StartY=25.15 StartZ=0 EndX=-22 EndY=16.75 EndZ=0
    g1: LineSegment StartX=-22 StartY=-25.15 StartZ=0 EndX=-8.25 EndY=-25.15 EndZ=0
    g2: LineSegment StartX=-8.25 StartY=-25.15 StartZ=0 EndX=-8.25 EndY=25.15 EndZ=0
    g3: LineSegment StartX=-22 StartY=25.15 StartZ=0 EndX=-8.25 EndY=25.15 EndZ=0
    g4: LineSegment StartX=-21.65 StartY=16.75 StartZ=0 EndX=-21.65 EndY=-16.75 EndZ=0
    g5: LineSegment StartX=-21.65 StartY=16.75 StartZ=0 EndX=-22 EndY=16.75 EndZ=0
    g6: LineSegment StartX=-21.65 StartY=-16.75 StartZ=0 EndX=-22 EndY=-16.75 EndZ=0
    g7: LineSegment StartX=-22 StartY=-16.75 StartZ=0 EndX=-22 EndY=-25.15 EndZ=0
  constraints (22):
    c: Coincident(g7,g1)
    c: Horizontal(g1)
    c: Coincident(g1,g2)
    c: Symmetric(g0,g7,g-1)
    c: Vertical(g2)
    c: Coincident(g3,g0)
    c: Horizontal(g3)
    c: DistanceY(g7,g0) = 50.3
    c: DistanceX(g3,g3) = 13.75
    c: DistanceX(g7,g-1) = 22
    c: Symmetric(g4,g4,g-1)
    c: DistanceY(g4,g4) = 33.5
    c: Coincident(g5,g4)
    c: Coincident(g6,g4)
    c: Horizontal(g6)
    c: Coincident(g5,g0)
    c: Coincident(g6,g7)
    c: Horizontal(g5)
    c: Distance(g5,g5) = 0.35
    c: Vertical(g0)
    c: Vertical(g7)
    c: Coincident(g2,g3)
FEATURE [PartDesign::Pad] Pad014
  BaseFeature = -> Pad013
  Direction = (0,0,1)
  Length = 3.5
  Length2 = 10
  Profile = -> Sketch030
  ReferenceAxis = -> Sketch030 [N_Axis]
  SideType = 0
  Suppressed = false
  Type = 0
  Type2 = 0
FEATURE [Sketcher::SketchObject] Sketch031
  ArcFitTolerance = 1e-06
  AttachmentSupport = -> [Pad014]
  ExternalGeometry = -> [Pad014]
  ExternalTypes = [0,0]
  FullyConstrained = true
  MakeInternals = false
  MapMode = 5
  Placement = pos=(0,0,3.5) rot=(0,0,1;0rad)
  _ExternalGeoVersion = 1
  sketch-geometry (4):
    g0: LineSegment StartX=-20.9 StartY=24.15 StartZ=0 EndX=-20.9 EndY=-24.15 EndZ=0
    g1: LineSegment StartX=-20.9 StartY=-24.15 StartZ=0 EndX=-9.25 EndY=-24.15 EndZ=0
    g2: LineSegment StartX=-9.25 StartY=-24.15 StartZ=0 EndX=-9.25 EndY=24.15 EndZ=0
    g3: LineSegment StartX=-9.25 StartY=24.15 StartZ=0 EndX=-20.9 EndY=24.15 EndZ=0
  constraints (11):
    c: Coincident(g0,g1)
    c: Coincident(g1,g2)
    c: Coincident(g2,g3)
    c: Coincident(g3,g0)
    c: Vertical(g0)
    c: Horizontal(g1)
    c: Horizontal(g3)
    c: Symmetric(g2,g1,g-1)
    c: DistanceY(g2,g-3) = 1
    c: DistanceX(g2,g-3) = 1
    c: DistanceX(g-4,g0) = 1.1
FEATURE [PartDesign::Pocket] Pocket003
  BaseFeature = -> Pad014
  Direction = (0,0,-1)
  Length = 1
  Length2 = 5
  Profile = -> Sketch031
  ReferenceAxis = -> Sketch031 [N_Axis]
  SideType = 0
  Suppressed = false
  Type = 0
  Type2 = 0
FEATURE [PartDesign::Body] Body008  label="Single Pass Dovetail Spacer"
  AllowCompound = false
  Group = -> [Sketch028,Pad013,Sketch030,Pad014,Sketch031,Pocket003]
  Origin = -> Origin016
  Tip = -> Pocket003
FEATURE [App::Point] Origin019  label="Origin024"
  Role = Origin
FEATURE [Sketcher::SketchObject] Sketch032
  ArcFitTolerance = 1e-06
  AttachmentSupport = -> [Origin018]
  ExternalTypes = [0]
  FullyConstrained = false
  MakeInternals = false
  MapMode = 5
  _ExternalGeoVersion = 1
  sketch-geometry (4):
    g0: LineSegment StartX=-45.8001 StartY=11.3 StartZ=0 EndX=-45.8001 EndY=-11.3 EndZ=0
    g1: LineSegment StartX=-45.8001 StartY=-11.3 StartZ=0 EndX=69.1999 EndY=-11.3 EndZ=0
    g2: LineSegment StartX=69.1999 StartY=-11.3 StartZ=0 EndX=69.1999 EndY=11.3 EndZ=0
    g3: LineSegment StartX=69.1999 StartY=11.3 StartZ=0 EndX=-45.8001 EndY=11.3 EndZ=0
  constraints (10):
    c: Coincident(g0,g1)
    c: Coincident(g1,g2)
    c: Coincident(g2,g3)
    c: Coincident(g3,g0)
    c: Vertical(g2)
    c: Horizontal(g1)
    c: Horizontal(g3)
    c: DistanceX(g3,g3) = 115
    c: DistanceY(g2,g2) = 22.6
    c: Symmetric(g0,g0,g-1)
FEATURE [PartDesign::Pad] Pad015
  Direction = (0,0,1)
  Length = 3.1
  Length2 = 10
  Profile = -> Sketch032
  ReferenceAxis = -> Sketch032 [N_Axis]
  SideType = 0
  Suppressed = false
  Type = 0
  Type2 = 0
FEATURE [Sketcher::SketchObject] Sketch033
  ArcFitTolerance = 1e-06
  AttachmentSupport = -> [Pad015]
  ExternalGeometry = -> [Pad015]
  ExternalTypes = [0,0]
  FullyConstrained = true
  MakeInternals = false
  MapMode = 5
  Placement = pos=(0,0,3.1) rot=(0,0,1;0rad)
  _ExternalGeoVersion = 1
  sketch-geometry (4):
    g0: LineSegment StartX=-45.8001 StartY=11.3 StartZ=0 EndX=-45.8001 EndY=-11.3 EndZ=0
    g1: LineSegment StartX=-45.8001 StartY=-11.3 StartZ=0 EndX=52.6999 EndY=-11.3 EndZ=0
    g2: LineSegment StartX=52.6999 StartY=-11.3 StartZ=0 EndX=52.6999 EndY=11.3 EndZ=0
    g3: LineSegment StartX=52.6999 StartY=11.3 StartZ=0 EndX=-45.8001 EndY=11.3 EndZ=0
  constraints (10):
    c: Coincident(g0,g1)
    c: Coincident(g1,g2)
    c: Coincident(g2,g3)
    c: Coincident(g3,g0)
    c: Vertical(g2)
    c: Horizontal(g1)
    c: Horizontal(g3)
    c: Coincident(g0,g-3)
    c: Coincident(g0,g-4)
    c: DistanceX(g3,g3) = 98.5
FEATURE [PartDesign::Pad] Pad016
  BaseFeature = -> Pad015
  Direction = (0,0,1)
  Length = 1.85
  Length2 = 10
  Profile = -> Sketch033
  ReferenceAxis = -> Sketch033 [N_Axis]
  SideType = 0
  Suppressed = false
  Type = 0
  Type2 = 0
FEATURE [Sketcher::SketchObject] Sketch034
  ArcFitTolerance = 1e-06
  AttachmentSupport = -> [Origin018]
  ExternalGeometry = -> [Sketch032]
  ExternalTypes = [0]
  FullyConstrained = true
  MakeInternals = false
  MapMode = 5
  _ExternalGeoVersion = 1
  sketch-geometry (1):
    g0: Circle CenterX=-13.3001 CenterY=0 CenterZ=0 NormalX=0 NormalY=0 NormalZ=1 AngleXU=0 Radius=3.25
  constraints (3):
    c: PointOnObject(g0,g-1)
    c: Diameter(g0) = 6.5
    c: DistanceX(g-3,g0) = 32.5
FEATURE [PartDesign::Pocket] Pocket004  label="Final"
  BaseFeature = -> Pad016
  Direction = (0,0,-1)
  Length = 5
  Length2 = 5
  Profile = -> Sketch034
  ReferenceAxis = -> Sketch034 [N_Axis]
  Reversed = true
  SideType = 0
  Suppressed = false
  Type = 1
  Type2 = 0
FEATURE [PartDesign::Body] Body009  label="Wrench"
  AllowCompound = false
  Group = -> [Sketch032,Pad015,Sketch033,Pad016,Sketch034,Pocket004]
  Origin = -> Origin018
  Tip = -> Pocket004
FEATURE [App::Point] Origin021  label="Origin027"
  Role = Origin
FEATURE [Sketcher::SketchObject] Sketch035
  ArcFitTolerance = 1e-06
  AttachmentSupport = -> [Origin020]
  ExternalTypes = [0]
  FullyConstrained = true
  MakeInternals = false
  MapMode = 5
  _ExternalGeoVersion = 1
  sketch-geometry (7):
    g0: LineSegment StartX=-55 StartY=7.5 StartZ=0 EndX=-55 EndY=-7.5 EndZ=0
    g1: LineSegment StartX=-55 StartY=-7.5 StartZ=0 EndX=55 EndY=-7.5 EndZ=0
    g2: LineSegment StartX=55 StartY=-7.5 StartZ=0 EndX=55 EndY=7.5 EndZ=0
    g3: LineSegment StartX=55 StartY=7.5 StartZ=0 EndX=-55 EndY=7.5 EndZ=0
    g4: GeomPoint [constr] X=0 Y=0 Z=0
    g5: Circle CenterX=-42 CenterY=0 CenterZ=0 NormalX=0 NormalY=0 NormalZ=1 AngleXU=0 Radius=3.5
    g6: Circle CenterX=42 CenterY=0 CenterZ=0 NormalX=0 NormalY=0 NormalZ=1 AngleXU=0 Radius=3.5
  constraints (17):
    c: Coincident(g0,g1)
    c: Coincident(g1,g2)
    c: Coincident(g2,g3)
    c: Coincident(g3,g0)
    c: Vertical(g0)
    c: Vertical(g2)
    c: Horizontal(g1)
    c: Horizontal(g3)
    c: Symmetric(g2,g0,g4)
    c: Coincident(g4,g-1)
    c: PointOnObject(g5,g-1)
    c: Symmetric(g5,g6,g-2)
    c: DistanceX(g5,g6) = 84
    c: DistanceX(g3,g3) = 110
    c: DistanceY(g2,g2) = 15
    c: Equal(g6,g5)
    c: Diameter(g6) = 7
FEATURE [PartDesign::Pad] Pad017
  Direction = (0,0,1)
  Length = 0.5
  Length2 = 10
  Profile = -> Sketch035
  ReferenceAxis = -> Sketch035 [N_Axis]
  SideType = 0
  Suppressed = false
  Type = 0
  Type2 = 0
FEATURE [PartDesign::Body] Body010  label="D4 Spacer"
  AllowCompound = false
  Group = -> [Sketch035,Pad017]
  Origin = -> Origin020
  Tip = -> Pad017
FEATURE [Mesh::Feature] FMT_M_and_T_Guide_8mmx30mm  label="FMT M and T Guide 8mmx30mm"
  Placement = pos=(0,0,0) rot=(0,0,1;3.14159rad)
FEATURE [Sketcher::SketchObject] Sketch036  label="Guide Outline"
  ArcFitTolerance = 1e-06
  ExternalTypes = [0]
  FullyConstrained = true
  MakeInternals = false
  Placement = pos=(0,0,3.1) rot=(0,0,1;0rad)
  _ExternalGeoVersion = 1
  expr: .Placement.Base.z = Spreadsheet.Base_Thickness
  sketch-geometry (148):
    g0: LineSegment StartX=26.0869 StartY=-22.875 StartZ=0 EndX=27.0797 EndY=-22.788 EndZ=0
    g1: LineSegment [constr] StartX=150.562 StartY=-11.4375 StartZ=0 EndX=151.559 EndY=-11.394 EndZ=0
    g2: LineSegment StartX=27.0797 StartY=-22.788 StartZ=0 EndX=28.0571 EndY=-22.5275 EndZ=0
    g3: LineSegment [constr] StartX=151.559 StartY=-11.394 StartZ=0 EndX=152.549 EndY=-11.2637 EndZ=0
    g4: LineSegment StartX=28.0571 StartY=-22.5275 StartZ=0 EndX=29.0119 EndY=-22.0956 EndZ=0
    g5: LineSegment [constr] StartX=152.549 StartY=-11.2637 StartZ=0 EndX=153.523 EndY=-11.0478 EndZ=0
    g6: LineSegment StartX=29.0119 StartY=-22.0956 StartZ=0 EndX=29.9373 EndY=-21.4955 EndZ=0
    g7: LineSegment [constr] StartX=153.523 StartY=-11.0478 StartZ=0 EndX=154.474 EndY=-10.7477 EndZ=0
    g8: LineSegment StartX=29.9373 StartY=-21.4955 StartZ=0 EndX=30.8267 EndY=-20.7318 EndZ=0
    g9: LineSegment [constr] StartX=154.474 StartY=-10.7477 StartZ=0 EndX=155.396 EndY=-10.3659 EndZ=0
    g10: LineSegment StartX=30.8267 StartY=-20.7318 StartZ=0 EndX=31.6743 EndY=-19.8103 EndZ=0
    g11: LineSegment [constr] StartX=155.396 StartY=-10.3659 StartZ=0 EndX=156.281 EndY=-9.90517 EndZ=0
    g12: LineSegment StartX=31.6743 StartY=-19.8103 StartZ=0 EndX=32.4744 EndY=-18.7381 EndZ=0
    g13: LineSegment [constr] StartX=156.281 StartY=-9.90517 StartZ=0 EndX=157.123 EndY=-9.36905 EndZ=0
    g14: LineSegment StartX=32.4744 StartY=-18.7381 StartZ=0 EndX=33.2218 EndY=-17.5233 EndZ=0
    g15: LineSegment [constr] StartX=157.123 StartY=-9.36905 StartZ=0 EndX=157.914 EndY=-8.76163 EndZ=0
    g16: LineSegment StartX=33.2218 StartY=-17.5233 StartZ=0 EndX=33.9119 EndY=-16.1751 EndZ=0
    g17: LineSegment [constr] StartX=157.914 StartY=-8.76163 StartZ=0 EndX=158.65 EndY=-8.08753 EndZ=0
    g18: LineSegment StartX=33.9119 StartY=-16.1751 StartZ=0 EndX=34.5405 EndY=-14.7038 EndZ=0
    g19: LineSegment [constr] StartX=158.65 StartY=-8.08753 StartZ=0 EndX=159.324 EndY=-7.35188 EndZ=0
    g20: LineSegment StartX=34.5405 StartY=-14.7038 StartZ=0 EndX=35.1038 EndY=-13.1206 EndZ=0
    g21: LineSegment [constr] StartX=159.324 StartY=-7.35188 StartZ=0 EndX=159.932 EndY=-6.56028 EndZ=0
    g22: LineSegment StartX=35.1038 StartY=-13.1206 StartZ=0 EndX=35.5986 EndY=-11.4375 EndZ=0
    g23: LineSegment [constr] StartX=159.932 StartY=-6.56028 StartZ=0 EndX=160.468 EndY=-5.71875 EndZ=0
    g24: LineSegment StartX=35.5986 StartY=-11.4375 StartZ=0 EndX=36.0219 EndY=-9.66739 EndZ=0
    g25: LineSegment [constr] StartX=160.468 StartY=-5.71875 StartZ=0 EndX=160.928 EndY=-4.8337 EndZ=0
    g26: LineSegment StartX=36.0219 StartY=-9.66739 StartZ=0 EndX=36.3715 EndY=-7.82371 EndZ=0
    g27: LineSegment [constr] StartX=160.928 StartY=-4.8337 StartZ=0 EndX=161.31 EndY=-3.91186 EndZ=0
    g28: LineSegment StartX=36.3715 StartY=-7.82371 StartZ=0 EndX=36.6453 EndY=-5.92049 EndZ=0
    g29: LineSegment [constr] StartX=161.31 StartY=-3.91186 StartZ=0 EndX=161.61 EndY=-2.96024 EndZ=0
    g30: LineSegment StartX=36.6453 StartY=-5.92049 StartZ=0 EndX=36.842 EndY=-3.9722 EndZ=0
    g31: LineSegment [constr] StartX=161.61 StartY=-2.96024 StartZ=0 EndX=161.826 EndY=-1.9861 EndZ=0
    g32: LineSegment StartX=36.842 StartY=-3.9722 StartZ=0 EndX=36.9605 EndY=-1.99369 EndZ=0
    g33: LineSegment [constr] StartX=161.826 StartY=-1.9861 StartZ=0 EndX=161.956 EndY=-0.996844 EndZ=0
    g34: LineSegment StartX=36.9605 StartY=-1.99369 StartZ=0 EndX=37 EndY=0 EndZ=0
    g35: LineSegment [constr] StartX=161.956 StartY=-0.996844 StartZ=0 EndX=162 EndY=0 EndZ=0
    g36: LineSegment StartX=37 StartY=0 StartZ=0 EndX=36.9605 EndY=1.99369 EndZ=0
    g37: LineSegment [constr] StartX=162 StartY=0 StartZ=0 EndX=161.956 EndY=0.996844 EndZ=0
    g38: LineSegment StartX=36.9605 StartY=1.99369 StartZ=0 EndX=36.842 EndY=3.9722 EndZ=0
    g39: LineSegment [constr] StartX=161.956 StartY=0.996844 StartZ=0 EndX=161.826 EndY=1.9861 EndZ=0
    g40: LineSegment StartX=36.842 StartY=3.9722 StartZ=0 EndX=36.6453 EndY=5.92049 EndZ=0
    g41: LineSegment [constr] StartX=161.826 StartY=1.9861 StartZ=0 EndX=161.61 EndY=2.96024 EndZ=0
    g42: LineSegment StartX=36.6453 StartY=5.92049 StartZ=0 EndX=36.3715 EndY=7.82371 EndZ=0
    g43: LineSegment [constr] StartX=161.61 StartY=2.96024 StartZ=0 EndX=161.31 EndY=3.91186 EndZ=0
    g44: LineSegment StartX=36.3715 StartY=7.82371 StartZ=0 EndX=36.0219 EndY=9.66739 EndZ=0
    g45: LineSegment [constr] StartX=161.31 StartY=3.91186 StartZ=0 EndX=160.928 EndY=4.8337 EndZ=0
    g46: LineSegment StartX=36.0219 StartY=9.66739 StartZ=0 EndX=35.5986 EndY=11.4375 EndZ=0
    g47: LineSegment [constr] StartX=160.928 StartY=4.8337 StartZ=0 EndX=160.468 EndY=5.71875 EndZ=0
    g48: LineSegment StartX=35.5986 StartY=11.4375 StartZ=0 EndX=35.1038 EndY=13.1206 EndZ=0
    g49: LineSegment [constr] StartX=160.468 StartY=5.71875 StartZ=0 EndX=159.932 EndY=6.56028 EndZ=0
    g50: LineSegment StartX=35.1038 StartY=13.1206 StartZ=0 EndX=34.5405 EndY=14.7038 EndZ=0
    g51: LineSegment [constr] StartX=159.932 StartY=6.56028 StartZ=0 EndX=159.324 EndY=7.35188 EndZ=0
    g52: LineSegment StartX=34.5405 StartY=14.7038 StartZ=0 EndX=33.9119 EndY=16.1751 EndZ=0
    g53: LineSegment [constr] StartX=159.324 StartY=7.35188 StartZ=0 EndX=158.65 EndY=8.08753 EndZ=0
    g54: LineSegment StartX=33.9119 StartY=16.1751 StartZ=0 EndX=33.2218 EndY=17.5233 EndZ=0
    g55: LineSegment [constr] StartX=158.65 StartY=8.08753 StartZ=0 EndX=157.914 EndY=8.76163 EndZ=0
    g56: LineSegment StartX=33.2218 StartY=17.5233 StartZ=0 EndX=32.4744 EndY=18.7381 EndZ=0
    g57: LineSegment [constr] StartX=157.914 StartY=8.76163 StartZ=0 EndX=157.123 EndY=9.36905 EndZ=0
    g58: LineSegment StartX=32.4744 StartY=18.7381 StartZ=0 EndX=31.6743 EndY=19.8103 EndZ=0
    g59: LineSegment [constr] StartX=157.123 StartY=9.36905 StartZ=0 EndX=156.281 EndY=9.90517 EndZ=0
    g60: LineSegment StartX=31.6743 StartY=19.8103 StartZ=0 EndX=30.8267 EndY=20.7318 EndZ=0
    g61: LineSegment [constr] StartX=156.281 StartY=9.90517 StartZ=0 EndX=155.396 EndY=10.3659 EndZ=0
    g62: LineSegment StartX=30.8267 StartY=20.7318 StartZ=0 EndX=29.9373 EndY=21.4955 EndZ=0
    g63: LineSegment [constr] StartX=155.396 StartY=10.3659 StartZ=0 EndX=154.474 EndY=10.7477 EndZ=0
    g64: LineSegment StartX=29.9373 StartY=21.4955 StartZ=0 EndX=29.0119 EndY=22.0956 EndZ=0
    g65: LineSegment [constr] StartX=154.474 StartY=10.7477 StartZ=0 EndX=153.523 EndY=11.0478 EndZ=0
    g66: LineSegment StartX=29.0119 StartY=22.0956 StartZ=0 EndX=28.0571 EndY=22.5275 EndZ=0
    g67: LineSegment [constr] StartX=153.523 StartY=11.0478 StartZ=0 EndX=152.549 EndY=11.2637 EndZ=0
    g68: LineSegment StartX=28.0571 StartY=22.5275 StartZ=0 EndX=27.0797 EndY=22.788 EndZ=0
    g69: LineSegment [constr] StartX=152.549 StartY=11.2637 StartZ=0 EndX=151.559 EndY=11.394 EndZ=0
    g70: LineSegment StartX=27.0797 StartY=22.788 StartZ=0 EndX=26.0869 EndY=22.875 EndZ=0
    g71: LineSegment [constr] StartX=151.559 StartY=11.394 StartZ=0 EndX=150.562 EndY=11.4375 EndZ=0
    g72: LineSegment StartX=26.0869 StartY=22.875 StartZ=0 EndX=-25.0381 EndY=22.875 EndZ=0
    g73: LineSegment [constr] StartX=150.562 StartY=11.4375 StartZ=0 EndX=99.4375 EndY=11.4375 EndZ=0
    g74: LineSegment StartX=-25.0381 StartY=22.875 StartZ=0 EndX=-26.039 EndY=22.788 EndZ=0
    g75: LineSegment [constr] StartX=99.4375 StartY=11.4375 StartZ=0 EndX=98.4407 EndY=11.394 EndZ=0
    g76: LineSegment StartX=-26.039 StartY=22.788 StartZ=0 EndX=-27.0401 EndY=22.5275 EndZ=0
    g77: LineSegment [constr] StartX=98.4407 StartY=11.394 StartZ=0 EndX=97.4514 EndY=11.2637 EndZ=0
    g78: LineSegment StartX=-27.0401 StartY=22.5275 StartZ=0 EndX=-28.0336 EndY=22.0956 EndZ=0
    g79: LineSegment [constr] StartX=97.4514 StartY=11.2637 StartZ=0 EndX=96.4773 EndY=11.0478 EndZ=0
    g80: LineSegment StartX=-28.0336 StartY=22.0956 StartZ=0 EndX=-29.0114 EndY=21.4955 EndZ=0
    g81: LineSegment [constr] StartX=96.4773 StartY=11.0478 StartZ=0 EndX=95.5256 EndY=10.7477 EndZ=0
    g82: LineSegment StartX=-29.0114 StartY=21.4955 StartZ=0 EndX=-29.9656 EndY=20.7318 EndZ=0
    g83: LineSegment [constr] StartX=95.5256 StartY=10.7477 StartZ=0 EndX=94.6038 EndY=10.3659 EndZ=0
    g84: LineSegment StartX=-29.9656 StartY=20.7318 StartZ=0 EndX=-30.8882 EndY=19.8103 EndZ=0
    g85: LineSegment [constr] StartX=94.6038 StartY=10.3659 StartZ=0 EndX=93.7188 EndY=9.90517 EndZ=0
    g86: LineSegment StartX=-30.8882 StartY=19.8103 StartZ=0 EndX=-31.7712 EndY=18.7381 EndZ=0
    g87: LineSegment [constr] StartX=93.7188 StartY=9.90517 StartZ=0 EndX=92.8772 EndY=9.36905 EndZ=0
    g88: LineSegment StartX=-31.7712 StartY=18.7381 StartZ=0 EndX=-32.6069 EndY=17.5233 EndZ=0
    g89: LineSegment [constr] StartX=92.8772 StartY=9.36905 StartZ=0 EndX=92.0856 EndY=8.76163 EndZ=0
    g90: LineSegment StartX=-32.6069 StartY=17.5233 StartZ=0 EndX=-33.3881 EndY=16.1751 EndZ=0
    g91: LineSegment [constr] StartX=92.0856 StartY=8.76163 StartZ=0 EndX=91.35 EndY=8.08753 EndZ=0
    g92: LineSegment StartX=-33.3881 StartY=16.1751 StartZ=0 EndX=-34.1077 EndY=14.7038 EndZ=0
    g93: LineSegment [constr] StartX=91.35 StartY=8.08753 StartZ=0 EndX=90.6759 EndY=7.35188 EndZ=0
    g94: LineSegment StartX=-34.1077 StartY=14.7038 StartZ=0 EndX=-34.7593 EndY=13.1206 EndZ=0
    g95: LineSegment [constr] StartX=90.6759 StartY=7.35188 StartZ=0 EndX=90.0684 EndY=6.56028 EndZ=0
    g96: LineSegment StartX=-34.7593 StartY=13.1206 StartZ=0 EndX=-35.3368 EndY=11.4375 EndZ=0
    g97: LineSegment [constr] StartX=90.0684 StartY=6.56028 StartZ=0 EndX=89.5323 EndY=5.71875 EndZ=0
    g98: LineSegment StartX=-35.3368 StartY=11.4375 StartZ=0 EndX=-35.8349 EndY=9.66739 EndZ=0
    g99: LineSegment [constr] StartX=89.5323 StartY=5.71875 StartZ=0 EndX=89.0716 EndY=4.8337 EndZ=0
    g100: LineSegment StartX=-35.8349 StartY=9.66739 StartZ=0 EndX=-36.249 EndY=7.82371 EndZ=0
    g101: LineSegment [constr] StartX=89.0716 StartY=4.8337 StartZ=0 EndX=88.6898 EndY=3.91186 EndZ=0
    g102: LineSegment StartX=-36.249 StartY=7.82371 StartZ=0 EndX=-36.5752 EndY=5.92049 EndZ=0
    g103: LineSegment [constr] StartX=88.6898 StartY=3.91186 StartZ=0 EndX=88.3897 EndY=2.96024 EndZ=0
    g104: LineSegment StartX=-36.5752 StartY=5.92049 StartZ=0 EndX=-36.8105 EndY=3.9722 EndZ=0
    g105: LineSegment [constr] StartX=88.3897 StartY=2.96024 StartZ=0 EndX=88.1738 EndY=1.9861 EndZ=0
    g106: LineSegment StartX=-36.8105 StartY=3.9722 StartZ=0 EndX=-36.9525 EndY=1.99369 EndZ=0
    g107: LineSegment [constr] StartX=88.1738 StartY=1.9861 StartZ=0 EndX=88.0435 EndY=0.996844 EndZ=0
    g108: LineSegment StartX=-36.9525 StartY=1.99369 StartZ=0 EndX=-37 EndY=0 EndZ=0
    g109: LineSegment [constr] StartX=88.0435 StartY=0.996844 StartZ=0 EndX=88 EndY=0 EndZ=0
    g110: LineSegment StartX=-37 StartY=0 StartZ=0 EndX=-36.9525 EndY=-1.99369 EndZ=0
    g111: LineSegment [constr] StartX=88 StartY=0 StartZ=0 EndX=88.0435 EndY=-0.996844 EndZ=0
    g112: LineSegment StartX=-36.9525 StartY=-1.99369 StartZ=0 EndX=-36.8105 EndY=-3.9722 EndZ=0
    g113: LineSegment [constr] StartX=88.0435 StartY=-0.996844 StartZ=0 EndX=88.1738 EndY=-1.9861 EndZ=0
    g114: LineSegment StartX=-36.8105 StartY=-3.9722 StartZ=0 EndX=-36.5752 EndY=-5.92049 EndZ=0
    g115: LineSegment [constr] StartX=88.1738 StartY=-1.9861 StartZ=0 EndX=88.3897 EndY=-2.96024 EndZ=0
    g116: LineSegment StartX=-36.5752 StartY=-5.92049 StartZ=0 EndX=-36.249 EndY=-7.82371 EndZ=0
    g117: LineSegment [constr] StartX=88.3897 StartY=-2.96024 StartZ=0 EndX=88.6898 EndY=-3.91186 EndZ=0
    g118: LineSegment StartX=-36.249 StartY=-7.82371 StartZ=0 EndX=-35.8349 EndY=-9.66739 EndZ=0
    g119: LineSegment [constr] StartX=88.6898 StartY=-3.91186 StartZ=0 EndX=89.0716 EndY=-4.8337 EndZ=0
    g120: LineSegment StartX=-35.8349 StartY=-9.66739 StartZ=0 EndX=-35.3368 EndY=-11.4375 EndZ=0
    g121: LineSegment [constr] StartX=89.0716 StartY=-4.8337 StartZ=0 EndX=89.5323 EndY=-5.71875 EndZ=0
    g122: LineSegment StartX=-35.3368 StartY=-11.4375 StartZ=0 EndX=-34.7593 EndY=-13.1206 EndZ=0
    g123: LineSegment [constr] StartX=89.5323 StartY=-5.71875 StartZ=0 EndX=90.0684 EndY=-6.56028 EndZ=0
    g124: LineSegment StartX=-34.7593 StartY=-13.1206 StartZ=0 EndX=-34.1077 EndY=-14.7038 EndZ=0
    g125: LineSegment [constr] StartX=90.0684 StartY=-6.56028 StartZ=0 EndX=90.6759 EndY=-7.35188 EndZ=0
    g126: LineSegment StartX=-34.1077 StartY=-14.7038 StartZ=0 EndX=-33.3881 EndY=-16.1751 EndZ=0
    g127: LineSegment [constr] StartX=90.6759 StartY=-7.35188 StartZ=0 EndX=91.35 EndY=-8.08753 EndZ=0
    g128: LineSegment StartX=-33.3881 StartY=-16.1751 StartZ=0 EndX=-32.6069 EndY=-17.5233 EndZ=0
    g129: LineSegment [constr] StartX=91.35 StartY=-8.08753 StartZ=0 EndX=92.0856 EndY=-8.76163 EndZ=0
    g130: LineSegment StartX=-32.6069 StartY=-17.5233 StartZ=0 EndX=-31.7712 EndY=-18.7381 EndZ=0
    g131: LineSegment [constr] StartX=92.0856 StartY=-8.76163 StartZ=0 EndX=92.8772 EndY=-9.36905 EndZ=0
    g132: LineSegment StartX=-31.7712 StartY=-18.7381 StartZ=0 EndX=-30.8882 EndY=-19.8103 EndZ=0
    g133: LineSegment [constr] StartX=92.8772 StartY=-9.36905 StartZ=0 EndX=93.7188 EndY=-9.90517 EndZ=0
    g134: LineSegment StartX=-30.8882 StartY=-19.8103 StartZ=0 EndX=-29.9656 EndY=-20.7318 EndZ=0
    g135: LineSegment [constr] StartX=93.7188 StartY=-9.90517 StartZ=0 EndX=94.6038 EndY=-10.3659 EndZ=0
    g136: LineSegment StartX=-29.9656 StartY=-20.7318 StartZ=0 EndX=-29.0114 EndY=-21.4955 EndZ=0
    g137: LineSegment [constr] StartX=94.6038 StartY=-10.3659 StartZ=0 EndX=95.5256 EndY=-10.7477 EndZ=0
    g138: LineSegment StartX=-29.0114 StartY=-21.4955 StartZ=0 EndX=-28.0336 EndY=-22.0956 EndZ=0
    g139: LineSegment [constr] StartX=95.5256 StartY=-10.7477 StartZ=0 EndX=96.4773 EndY=-11.0478 EndZ=0
    g140: LineSegment StartX=-28.0336 StartY=-22.0956 StartZ=0 EndX=-27.0401 EndY=-22.5275 EndZ=0
    g141: LineSegment [constr] StartX=96.4773 StartY=-11.0478 StartZ=0 EndX=97.4514 EndY=-11.2637 EndZ=0
    g142: LineSegment StartX=-27.0401 StartY=-22.5275 StartZ=0 EndX=-26.039 EndY=-22.788 EndZ=0
    g143: LineSegment [constr] StartX=97.4514 StartY=-11.2637 StartZ=0 EndX=98.4407 EndY=-11.394 EndZ=0
    g144: LineSegment StartX=-26.039 StartY=-22.788 StartZ=0 EndX=-25.0381 EndY=-22.875 EndZ=0
    g145: LineSegment [constr] StartX=98.4407 StartY=-11.394 StartZ=0 EndX=99.4375 EndY=-11.4375 EndZ=0
    g146: LineSegment StartX=-25.0381 StartY=-22.875 StartZ=0 EndX=26.0869 EndY=-22.875 EndZ=0
    g147: LineSegment [constr] StartX=99.4375 StartY=-11.4375 StartZ=0 EndX=150.562 EndY=-11.4375 EndZ=0
  constraints (296):
    c: Block(g0)
    c: Block(g1)
    c: Block(g2)
    c: Coincident(g0,g2)
    c: Block(g3)
    c: Coincident(g1,g3)
    c: Block(g4)
    c: Coincident(g2,g4)
    c: Block(g5)
    c: Coincident(g3,g5)
    c: Block(g6)
    c: Coincident(g4,g6)
    c: Block(g7)
    c: Coincident(g5,g7)
    c: Block(g8)
    c: Coincident(g6,g8)
    c: Block(g9)
    c: Coincident(g7,g9)
    c: Block(g10)
    c: Coincident(g8,g10)
    c: Block(g11)
    c: Coincident(g9,g11)
    c: Block(g12)
    c: Coincident(g10,g12)
    c: Block(g13)
    c: Coincident(g11,g13)
    c: Block(g14)
    c: Coincident(g12,g14)
    c: Block(g15)
    c: Coincident(g13,g15)
    c: Block(g16)
    c: Coincident(g14,g16)
    c: Block(g17)
    c: Coincident(g15,g17)
    c: Block(g18)
    c: Coincident(g16,g18)
    c: Block(g19)
    c: Coincident(g17,g19)
    c: Block(g20)
    c: Coincident(g18,g20)
    c: Block(g21)
    c: Coincident(g19,g21)
    c: Block(g22)
    c: Coincident(g20,g22)
    c: Block(g23)
    c: Coincident(g21,g23)
    c: Block(g24)
    c: Coincident(g22,g24)
    c: Block(g25)
    c: Coincident(g23,g25)
    c: Block(g26)
    c: Coincident(g24,g26)
    c: Block(g27)
    c: Coincident(g25,g27)
    c: Block(g28)
    c: Coincident(g26,g28)
    c: Block(g29)
    c: Coincident(g27,g29)
    c: Block(g30)
    c: Coincident(g28,g30)
    c: Block(g31)
    c: Coincident(g29,g31)
    c: Block(g32)
    c: Coincident(g30,g32)
    c: Block(g33)
    c: Coincident(g31,g33)
    c: Block(g34)
    c: Coincident(g32,g34)
    c: Block(g35)
    c: Coincident(g33,g35)
    c: Block(g36)
    c: Coincident(g34,g36)
    c: Block(g37)
    c: Coincident(g35,g37)
    c: Block(g38)
    c: Coincident(g36,g38)
    c: Block(g39)
    c: Coincident(g37,g39)
    c: Block(g40)
    c: Coincident(g38,g40)
    c: Block(g41)
    c: Coincident(g39,g41)
    c: Block(g42)
    c: Coincident(g40,g42)
    c: Block(g43)
    c: Coincident(g41,g43)
    c: Block(g44)
    c: Coincident(g42,g44)
    c: Block(g45)
    c: Coincident(g43,g45)
    c: Block(g46)
    c: Coincident(g44,g46)
    c: Block(g47)
    c: Coincident(g45,g47)
    c: Block(g48)
    c: Coincident(g46,g48)
    c: Block(g49)
    c: Coincident(g47,g49)
    c: Block(g50)
    c: Coincident(g48,g50)
    c: Block(g51)
    c: Coincident(g49,g51)
    c: Block(g52)
    c: Coincident(g50,g52)
    c: Block(g53)
    c: Coincident(g51,g53)
    c: Block(g54)
    c: Coincident(g52,g54)
    c: Block(g55)
    c: Coincident(g53,g55)
    c: Block(g56)
    c: Coincident(g54,g56)
    c: Block(g57)
    c: Coincident(g55,g57)
    c: Block(g58)
    c: Coincident(g56,g58)
    c: Block(g59)
    c: Coincident(g57,g59)
    c: Block(g60)
    c: Coincident(g58,g60)
    c: Block(g61)
    c: Coincident(g59,g61)
    c: Block(g62)
    c: Coincident(g60,g62)
    c: Block(g63)
    c: Coincident(g61,g63)
    c: Block(g64)
    c: Coincident(g62,g64)
    c: Block(g65)
    c: Coincident(g63,g65)
    c: Block(g66)
    c: Coincident(g64,g66)
    c: Block(g67)
    c: Coincident(g65,g67)
    c: Block(g68)
    c: Coincident(g66,g68)
    c: Block(g69)
    c: Coincident(g67,g69)
    c: Block(g70)
    c: Coincident(g68,g70)
    c: Block(g71)
    c: Coincident(g69,g71)
    c: Block(g72)
    c: Coincident(g70,g72)
    c: Block(g73)
    c: Coincident(g71,g73)
    c: Block(g74)
    c: Coincident(g72,g74)
    c: Block(g75)
    c: Coincident(g73,g75)
    c: Block(g76)
    c: Coincident(g74,g76)
    c: Block(g77)
    c: Coincident(g75,g77)
    c: Block(g78)
    c: Coincident(g76,g78)
    c: Block(g79)
    c: Coincident(g77,g79)
    c: Block(g80)
    c: Coincident(g78,g80)
    c: Block(g81)
    c: Coincident(g79,g81)
    c: Block(g82)
    c: Coincident(g80,g82)
    c: Block(g83)
    c: Coincident(g81,g83)
    c: Block(g84)
    c: Coincident(g82,g84)
    c: Block(g85)
    c: Coincident(g83,g85)
    c: Block(g86)
    c: Coincident(g84,g86)
    c: Block(g87)
    c: Coincident(g85,g87)
    c: Block(g88)
    c: Coincident(g86,g88)
    c: Block(g89)
    c: Coincident(g87,g89)
    c: Block(g90)
    c: Coincident(g88,g90)
    c: Block(g91)
    c: Coincident(g89,g91)
    c: Block(g92)
    c: Coincident(g90,g92)
    c: Block(g93)
    c: Coincident(g91,g93)
    c: Block(g94)
    c: Coincident(g92,g94)
    c: Block(g95)
    c: Coincident(g93,g95)
    c: Block(g96)
    c: Coincident(g94,g96)
    c: Block(g97)
    c: Coincident(g95,g97)
    c: Block(g98)
    c: Coincident(g96,g98)
    c: Block(g99)
    c: Coincident(g97,g99)
    c: Block(g100)
    c: Coincident(g98,g100)
    c: Block(g101)
    c: Coincident(g99,g101)
    c: Block(g102)
    c: Coincident(g100,g102)
    c: Block(g103)
    c: Coincident(g101,g103)
    c: Block(g104)
    c: Coincident(g102,g104)
    c: Block(g105)
    c: Coincident(g103,g105)
    c: Block(g106)
    c: Coincident(g104,g106)
    c: Block(g107)
    c: Coincident(g105,g107)
    c: Block(g108)
    c: Coincident(g106,g108)
    c: Block(g109)
    c: Coincident(g107,g109)
    c: Block(g110)
    c: Coincident(g108,g110)
    c: Block(g111)
    c: Coincident(g109,g111)
    c: Block(g112)
    c: Coincident(g110,g112)
    c: Block(g113)
    c: Coincident(g111,g113)
    c: Block(g114)
    c: Coincident(g112,g114)
    c: Block(g115)
    c: Coincident(g113,g115)
    c: Block(g116)
    c: Coincident(g114,g116)
    c: Block(g117)
    c: Coincident(g115,g117)
    c: Block(g118)
    c: Coincident(g116,g118)
    c: Block(g119)
    c: Coincident(g117,g119)
    c: Block(g120)
    c: Coincident(g118,g120)
    c: Block(g121)
    c: Coincident(g119,g121)
    c: Block(g122)
    c: Coincident(g120,g122)
    c: Block(g123)
    c: Coincident(g121,g123)
    c: Block(g124)
    c: Coincident(g122,g124)
    c: Block(g125)
    c: Coincident(g123,g125)
    c: Block(g126)
    c: Coincident(g124,g126)
    c: Block(g127)
    c: Coincident(g125,g127)
    c: Block(g128)
    c: Coincident(g126,g128)
    c: Block(g129)
    c: Coincident(g127,g129)
    c: Block(g130)
    c: Coincident(g128,g130)
    c: Block(g131)
    c: Coincident(g129,g131)
    c: Block(g132)
    c: Coincident(g130,g132)
    c: Block(g133)
    c: Coincident(g131,g133)
    c: Block(g134)
    c: Coincident(g132,g134)
    c: Block(g135)
    c: Coincident(g133,g135)
    c: Block(g136)
    c: Coincident(g134,g136)
    c: Block(g137)
    c: Coincident(g135,g137)
    c: Block(g138)
    c: Coincident(g136,g138)
    c: Block(g139)
    c: Coincident(g137,g139)
    c: Block(g140)
    c: Coincident(g138,g140)
    c: Block(g141)
    c: Coincident(g139,g141)
    c: Block(g142)
    c: Coincident(g140,g142)
    c: Block(g143)
    c: Coincident(g141,g143)
    c: Block(g144)
    c: Coincident(g142,g144)
    c: Block(g145)
    c: Coincident(g143,g145)
    c: Block(g146)
    c: Coincident(g144,g146)
    c: Coincident(g146,g0)
    c: Block(g147)
    c: Coincident(g145,g147)
    c: Coincident(g147,g1)
FEATURE [App::Point] Origin023  label="Origin030"
  Role = Origin
FEATURE [PartDesign::Pad] Pad018
  Direction = (0,0,1)
  Length = 6.6
  Length2 = 10
  Placement = pos=(0,0,3.1) rot=(0,0,1;0rad)
  Profile = -> Sketch036
  ReferenceAxis = -> Sketch036 [N_Axis]
  SideType = 0
  Suppressed = false
  TaperAngle = -9.22
  Type = 0
  Type2 = 0
  expr: Length = Spreadsheet.Upper_Plane - Spreadsheet.Base_Thickness
  expr: TaperAngle = -Spreadsheet.Pin_Angle
FEATURE [Sketcher::SketchObject] Sketch037
  ArcFitTolerance = 1e-06
  AttachmentSupport = -> [DatumPlane002]
  ExternalTypes = [0]
  FullyConstrained = false
  MakeInternals = false
  MapMode = 5
  Placement = pos=(0,0,3.1) rot=(0,0,1;0rad)
  _ExternalGeoVersion = 1
  sketch-geometry (6):
    g0: LineSegment StartX=-0.5 StartY=14.4396 StartZ=0 EndX=-0.5 EndY=-14.4396 EndZ=0
    g1: LineSegment StartX=-0.5 StartY=-14.4396 StartZ=0 EndX=0.5 EndY=-14.4396 EndZ=0
    g2: LineSegment StartX=0.5 StartY=-14.4396 StartZ=0 EndX=0.5 EndY=14.4396 EndZ=0
    g3: LineSegment StartX=0.5 StartY=14.4396 StartZ=0 EndX=-0.5 EndY=14.4396 EndZ=0
    g4: GeomPoint [constr] X=0 Y=1e-16 Z=0
    g5: Circle CenterX=4.63741 CenterY=3.99915 CenterZ=0 NormalX=0 NormalY=0 NormalZ=1 AngleXU=0 Radius=0.5
  constraints (12):
    c: Coincident(g0,g1)
    c: Coincident(g1,g2)
    c: Coincident(g2,g3)
    c: Coincident(g3,g0)
    c: Vertical(g0)
    c: Horizontal(g1)
    c: Horizontal(g3)
    c: Symmetric(g2,g0,g4)
    c: PointOnObject(g4,g-2)
    c: Distance(g3,g3) = 1
    c: Symmetric(g1,g2,g-1)
    c: Diameter(g5) = 1
FEATURE [PartDesign::Body] Body011  label="Guide"
  AllowCompound = false
  Group = -> [Sketch036,Pad018,Sketch037]
  Origin = -> Origin022
  Tip = -> Pad018
FEATURE [Part::Cut] Cut003  label="Guide with Slot"
  Base = -> Body011
  Tool = -> Loft
FEATURE [Part::Fuse] Fusion009  label="M & T Guide"
  Base = -> Fusion007
  Tool = -> Cut003
FEATURE [Part::Fuse] Fusion011  label="Y Tenon"
  Base = -> Fusion007
  Tool = -> Body005
FEATURE [Mesh::Feature] FMT_M_and_T_Guide_6mmx35mm  label="FMT M and T Guide 6mmx35mm"
  Placement = pos=(0,0,0) rot=(0,0,1;3.14159rad)
note: 4 file-system paths scrubbed to <path> (originals preserved in the JSON sidecar)
